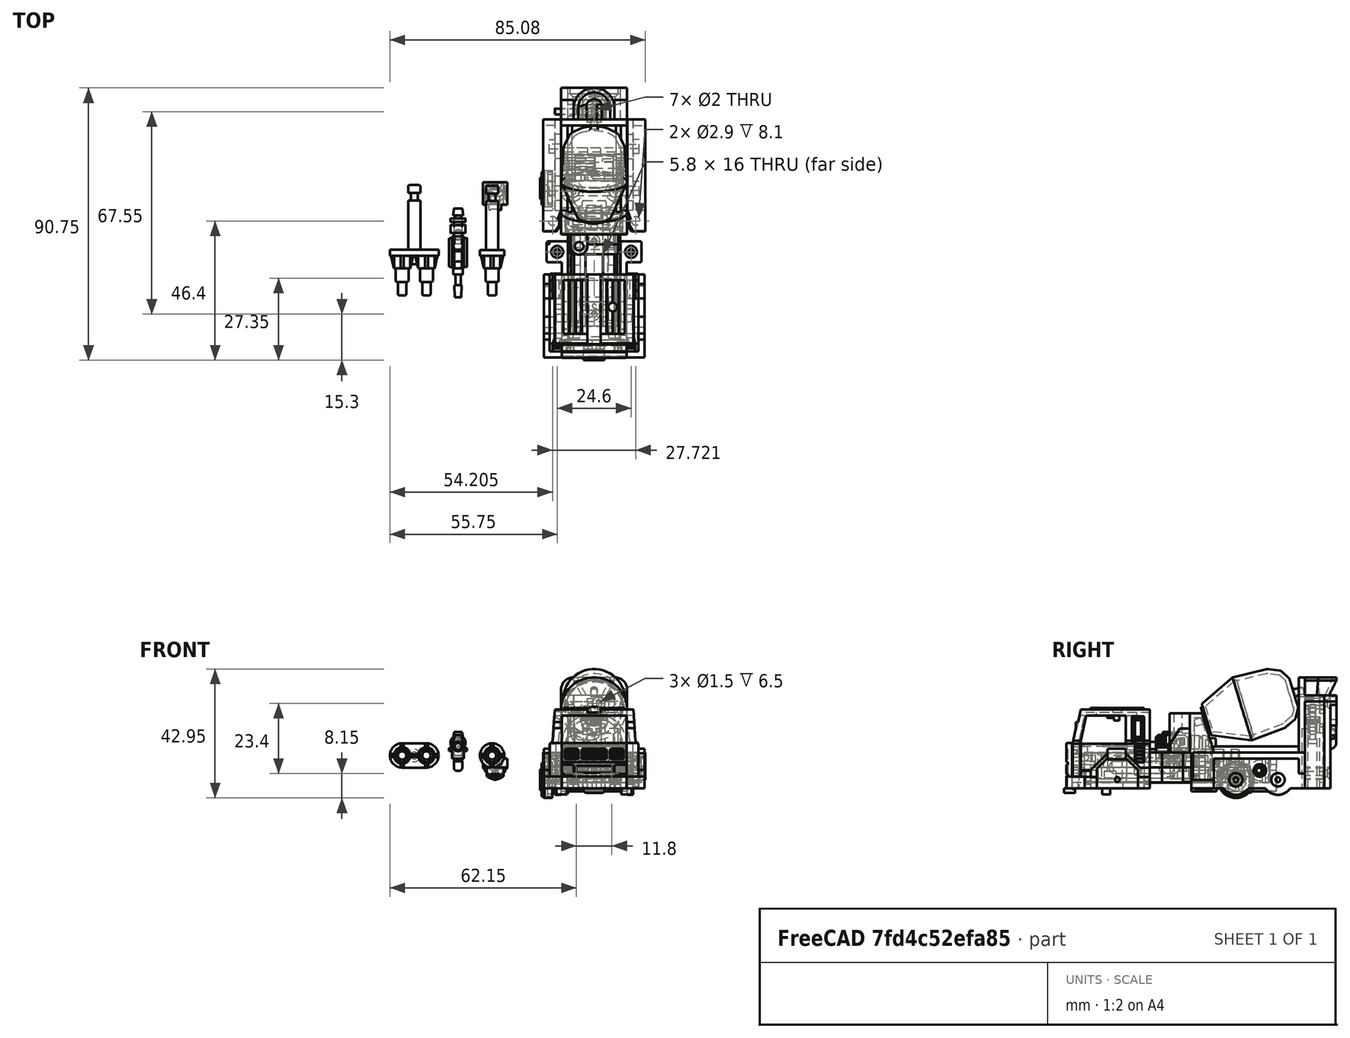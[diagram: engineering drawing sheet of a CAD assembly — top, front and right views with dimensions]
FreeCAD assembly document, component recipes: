
FREECAD ASSEMBLY — COMPONENT RECIPES ("MixMaster")

This assembly document has 25 components, labeled P0..P24 below (a component is one placed body or linked part). 24 of them carry a construction recipe — the FreeCAD feature program that regenerates the part from scratch, quoted from this document or its linked companion documents; the rest are supplied as boundary geometry only. No exploded tour is included for this assembly.
NOTE — document 2 of 4 of this assembly tour. The two overview renders and the header above are repeated from document 1; the component sections below continue where the previous document stopped.
COMPONENT P6 — recipe-attached ("top", modeled in this document).
Construction recipe (the document's own serialized feature program — sketch geometry with constraints, then the solid features built on it; lengths are millimeters unless a unit is written):

FEATURE [PartDesign::SubShapeBinder] Binder007
  BindCopyOnChange = 0
  BindMode = 2
  ClaimChildren = false
  Fuse = false
  MakeFace = true
  OffsetFill = false
  OffsetIntersection = false
  OffsetJoinType = 0
  OffsetOpenResult = false
  PartialLoad = false
  Refine = true
  Relative = true
  _Version = 2
FEATURE [Sketcher::SketchObject] Sketch141
  ArcFitTolerance = 1e-06
  AttachmentSupport = -> [Binder007]
  ExternalGeometry = -> [Binder007]
  FullyConstrained = true
  MakeInternals = false
  MapMode = 5
  Placement = pos=(5.89e-14,23,-1.557e-13) rot=(0,0.707107,0.707107;3.14159rad)
  sketch-geometry (8):
    g0: LineSegment StartX=-19.8 StartY=-11 StartZ=0 EndX=-19.8 EndY=18 EndZ=0
    g1: LineSegment StartX=-19.8 StartY=18 StartZ=0 EndX=-22 EndY=18 EndZ=0
    g2: LineSegment StartX=-19.8 StartY=-11 StartZ=0 EndX=-2.2 EndY=-11 EndZ=0
    g3: LineSegment StartX=-2.2 StartY=-11 StartZ=0 EndX=-2.2 EndY=18 EndZ=0
    g4: LineSegment StartX=-2.2 StartY=18 StartZ=0 EndX=0 EndY=18 EndZ=0
    g5: LineSegment StartX=0 StartY=18 StartZ=0 EndX=0 EndY=20 EndZ=0
    g6: LineSegment StartX=0 StartY=20 StartZ=0 EndX=-22 EndY=20 EndZ=0
    g7: LineSegment StartX=-22 StartY=20 StartZ=0 EndX=-22 EndY=18 EndZ=0
  constraints (21):
    c: Coincident(g0,g-3)
    c: Coincident(g0,g-3)
    c: Coincident(g1,g0)
    c: Horizontal(g1)
    c: DistanceX(g1,g1) = 2.2
    c: Coincident(g2,g0)
    c: Horizontal(g2)
    c: DistanceX(g2,g2) = 17.6
    c: Coincident(g3,g2)
    c: Vertical(g3)
    c: DistanceY(g3,g3) = 29
    c: Coincident(g4,g3)
    c: Horizontal(g4)
    c: DistanceX(g4,g4) = 2.2
    c: Coincident(g5,g4)
    c: Vertical(g5)
    c: DistanceY(g5,g5) = 2
    c: Coincident(g6,g5)
    c: Coincident(g6,g-4)
    c: Coincident(g7,g6)
    c: Coincident(g7,g1)
FEATURE [PartDesign::Pad] Pad114
  Direction = (2.6e-15,1,-6.7e-15)
  Length = 2
  Length2 = 10
  Profile = -> Sketch141
  ReferenceAxis = -> Sketch141 [N_Axis]
  Refine = true
  Suppressed = false
  Type = 0
FEATURE [Sketcher::SketchObject] Sketch142
  ArcFitTolerance = 1e-06
  AttachmentSupport = -> [Pad114]
  ExternalGeometry = -> [Pad114]
  FullyConstrained = true
  MakeInternals = false
  MapMode = 5
  Placement = pos=(5.82e-14,23,-1.559e-13) rot=(1,0,0;1.5708rad)
  sketch-geometry (8):
    g0: LineSegment StartX=14.75 StartY=-11 StartZ=0 EndX=14.75 EndY=10.5 EndZ=0
    g1: LineSegment StartX=14.75 StartY=10.5 StartZ=0 EndX=13.25 EndY=10.5 EndZ=0
    g2: LineSegment StartX=13.25 StartY=10.5 StartZ=0 EndX=13.25 EndY=-11 EndZ=0
    g3: LineSegment StartX=13.25 StartY=-11 StartZ=0 EndX=14.75 EndY=-11 EndZ=0
    g4: LineSegment StartX=8.75 StartY=-11 StartZ=0 EndX=8.75 EndY=10.5 EndZ=0
    g5: LineSegment StartX=8.75 StartY=10.5 StartZ=0 EndX=7.25 EndY=10.5 EndZ=0
    g6: LineSegment StartX=7.25 StartY=10.5 StartZ=0 EndX=7.25 EndY=-11 EndZ=0
    g7: LineSegment StartX=7.25 StartY=-11 StartZ=0 EndX=8.75 EndY=-11 EndZ=0
  constraints (24):
    c: PointOnObject(g0,g-3)
    c: Vertical(g0)
    c: Coincident(g1,g0)
    c: Horizontal(g1)
    c: Coincident(g2,g1)
    c: PointOnObject(g2,g-3)
    c: Vertical(g2)
    c: Coincident(g3,g2)
    c: Coincident(g3,g0)
    c: DistanceX(g0,g-3) = 5.05
    c: DistanceX(g2,g0) = 1.5
    c: DistanceY(g2,g2) = 21.5
    c: Coincident(g4,g5)
    c: Coincident(g5,g6)
    c: Coincident(g6,g7)
    c: Coincident(g7,g4)
    c: Vertical(g4)
    c: Vertical(g6)
    c: Horizontal(g5)
    c: Horizontal(g7)
    c: PointOnObject(g4,g-3)
    c: DistanceX(g7,g7) = 1.5
    c: DistanceX(g4,g2) = 4.5
    c: DistanceY(g6,g6) = 21.5
FEATURE [PartDesign::Pad] Pad115
  BaseFeature = -> Pad114
  Direction = (-2.5e-15,-1,6.7e-15)
  Length = 1.5
  Length2 = 10
  Profile = -> Sketch142
  ReferenceAxis = -> Sketch142 [N_Axis]
  Refine = true
  Suppressed = false
  Type = 0
FEATURE [Sketcher::SketchObject] Sketch143
  ArcFitTolerance = 1e-06
  AttachmentSupport = -> [Pad115]
  ExternalGeometry = -> [Pad115]
  FullyConstrained = true
  MakeInternals = false
  MapMode = 5
  Placement = pos=(5.82e-14,23,-1.559e-13) rot=(1,0,0;1.5708rad)
  sketch-geometry (8):
    g0: LineSegment StartX=11.75 StartY=-11 StartZ=0 EndX=10.25 EndY=-11 EndZ=0
    g1: LineSegment StartX=10.25 StartY=-11 StartZ=0 EndX=10.25 EndY=9 EndZ=0
    g2: LineSegment StartX=10.25 StartY=9 StartZ=0 EndX=8.75 EndY=9 EndZ=0
    g3: LineSegment StartX=8.75 StartY=9 StartZ=0 EndX=8.75 EndY=10.5 EndZ=0
    g4: LineSegment StartX=8.75 StartY=10.5 StartZ=0 EndX=13.25 EndY=10.5 EndZ=0
    g5: LineSegment StartX=13.25 StartY=10.5 StartZ=0 EndX=13.25 EndY=9 EndZ=0
    g6: LineSegment StartX=13.25 StartY=9 StartZ=0 EndX=11.75 EndY=9 EndZ=0
    g7: LineSegment StartX=11.75 StartY=9 StartZ=0 EndX=11.75 EndY=-11 EndZ=0
  constraints (22):
    c: PointOnObject(g0,g-3)
    c: PointOnObject(g0,g-3)
    c: Coincident(g1,g0)
    c: Vertical(g1)
    c: Coincident(g2,g1)
    c: PointOnObject(g2,g-4)
    c: Horizontal(g2)
    c: Coincident(g3,g2)
    c: Coincident(g3,g-4)
    c: Coincident(g4,g3)
    c: Coincident(g4,g-5)
    c: Coincident(g5,g4)
    c: PointOnObject(g5,g-5)
    c: Coincident(g6,g5)
    c: Horizontal(g6)
    c: Coincident(g7,g6)
    c: Coincident(g7,g0)
    c: Vertical(g7)
    c: DistanceX(g0,g0) = 1.5
    c: DistanceX(g-4,g0) = 1.5
    c: DistanceY(g3,g3) = 1.5
    c: DistanceY(g5,g5) = 1.5
FEATURE [PartDesign::Pad] Pad116
  BaseFeature = -> Pad115
  Direction = (-2.5e-15,-1,6.7e-15)
  Length = 0.5
  Length2 = 10
  Profile = -> Sketch143
  ReferenceAxis = -> Sketch143 [N_Axis]
  Refine = true
  Suppressed = false
  Type = 0
FEATURE [Sketcher::SketchObject] Sketch144
  ArcFitTolerance = 1e-06
  AttachmentSupport = -> [Pad116]
  ExternalGeometry = -> [Pad116]
  FullyConstrained = true
  MakeInternals = false
  MapMode = 5
  Placement = pos=(5.82e-14,23,-1.559e-13) rot=(1,0,0;1.5708rad)
  sketch-geometry (12):
    g0: LineSegment StartX=5.7 StartY=-11 StartZ=0 EndX=5.7 EndY=-9 EndZ=0
    g1: LineSegment StartX=5.7 StartY=-9 StartZ=0 EndX=4.2 EndY=-9 EndZ=0
    g2: LineSegment StartX=4.2 StartY=-9 StartZ=0 EndX=4.2 EndY=-11 EndZ=0
    g3: LineSegment StartX=4.2 StartY=-11 StartZ=0 EndX=5.7 EndY=-11 EndZ=0
    g4: LineSegment StartX=17.8 StartY=-11 StartZ=0 EndX=17.8 EndY=-9 EndZ=0
    g5: LineSegment StartX=17.8 StartY=-9 StartZ=0 EndX=16.3 EndY=-9 EndZ=0
    g6: LineSegment StartX=16.3 StartY=-9 StartZ=0 EndX=16.3 EndY=-11 EndZ=0
    g7: LineSegment StartX=16.3 StartY=-11 StartZ=0 EndX=17.8 EndY=-11 EndZ=0
    g8: LineSegment StartX=2.2 StartY=16.9 StartZ=0 EndX=2.2 EndY=9.5 EndZ=0
    g9: LineSegment StartX=2.2 StartY=9.5 StartZ=0 EndX=4.2 EndY=9.5 EndZ=0
    g10: LineSegment StartX=4.2 StartY=9.5 StartZ=0 EndX=4.2 EndY=16.9 EndZ=0
    g11: LineSegment StartX=4.2 StartY=16.9 StartZ=0 EndX=2.2 EndY=16.9 EndZ=0
  constraints (36):
    c: Coincident(g0,g1)
    c: Coincident(g1,g2)
    c: Coincident(g2,g3)
    c: Coincident(g3,g0)
    c: Vertical(g0)
    c: Vertical(g2)
    c: Horizontal(g1)
    c: Horizontal(g3)
    c: PointOnObject(g0,g-3)
    c: Coincident(g4,g5)
    c: Coincident(g5,g6)
    c: Coincident(g6,g7)
    c: Coincident(g7,g4)
    c: Vertical(g4)
    c: Vertical(g6)
    c: Horizontal(g5)
    c: Horizontal(g7)
    c: Coincident(g8,g9)
    c: Coincident(g9,g10)
    c: Coincident(g10,g11)
    c: Coincident(g11,g8)
    c: Vertical(g8)
    c: Vertical(g10)
    c: Horizontal(g9)
    c: Horizontal(g11)
    c: PointOnObject(g8,g-5)
    c: DistanceY(g8,g-5) = 1.1
    c: DistanceY(g8,g8) = 7.4
    c: DistanceX(g11,g11) = 2
    c: DistanceX(g3,g3) = 1.5
    c: DistanceY(g0,g0) = 2
    c: DistanceY(g6,g6) = 2
    c: DistanceX(g7,g7) = 1.5
    c: PointOnObject(g4,g-4)
    c: DistanceX(g-5,g2) = 2
    c: DistanceX(g4,g-4) = 2
FEATURE [PartDesign::Pad] Pad117
  BaseFeature = -> Pad116
  Direction = (-2.5e-15,-1,6.7e-15)
  Length = 1.5
  Length2 = 10
  Profile = -> Sketch144
  ReferenceAxis = -> Sketch144 [N_Axis]
  Refine = true
  Suppressed = false
  Type = 0
FEATURE [Sketcher::SketchObject] Sketch145
  ArcFitTolerance = 1e-06
  AttachmentSupport = -> [Pad117]
  ExternalGeometry = -> [Pad117]
  FullyConstrained = true
  MakeInternals = false
  MapMode = 5
  Placement = pos=(5.82e-14,23,-1.559e-13) rot=(1,0,0;1.5708rad)
  sketch-geometry (12):
    g0: LineSegment StartX=4.2 StartY=20 StartZ=0 EndX=4.2 EndY=18 EndZ=0
    g1: LineSegment StartX=4.2 StartY=18 StartZ=0 EndX=8.7 EndY=18 EndZ=0
    g2: LineSegment StartX=8.7 StartY=18 StartZ=0 EndX=8.7 EndY=19 EndZ=0
    g3: LineSegment StartX=8.7 StartY=19 StartZ=0 EndX=10.95 EndY=19 EndZ=0
    g4: LineSegment StartX=11.95 StartY=20 StartZ=0 EndX=4.2 EndY=20 EndZ=0
    g5: ArcOfCircle CenterX=10.95 CenterY=20 CenterZ=0 NormalX=0 NormalY=0 NormalZ=1 AngleXU=0 Radius=1 StartAngle=4.71239 EndAngle=6.28319
    g6: GeomPoint [constr] X=10.95 Y=19 Z=0
    g7: LineSegment StartX=17.8 StartY=20 StartZ=0 EndX=13.55 EndY=20 EndZ=0
    g8: LineSegment StartX=15.55 StartY=18 StartZ=0 EndX=17.8 EndY=18 EndZ=0
    g9: LineSegment StartX=17.8 StartY=18 StartZ=0 EndX=17.8 EndY=20 EndZ=0
    g10: ArcOfCircle CenterX=15.55 CenterY=20 CenterZ=0 NormalX=0 NormalY=0 NormalZ=1 AngleXU=0 Radius=2 StartAngle=3.14159 EndAngle=4.71239
    g11: GeomPoint [constr] X=15.55 Y=18 Z=0
  constraints (32):
    c: PointOnObject(g0,g-3)
    c: Vertical(g0)
    c: Coincident(g1,g0)
    c: Horizontal(g1)
    c: Coincident(g2,g1)
    c: Coincident(g3,g2)
    c: Horizontal(g3)
    c: Coincident(g4,g0)
    c: Horizontal(g4)
    c: Tangent(g3,g5) = -1.5708
    c: Coincident(g8,g9)
    c: Coincident(g9,g7)
    c: Horizontal(g7)
    c: Horizontal(g8)
    c: Vertical(g9)
    c: PointOnObject(g7,g-3)
    c: Tangent(g8,g10) = -1.5708
    c: DistanceY(g9,g9) = 2
    c: DistanceY(g0,g0) = 2
    c: Vertical(g2)
    c: DistanceX(g-3,g0) = 4.2
    c: DistanceX(g7,g-3) = 4.2
    c: Coincident(g10,g7)
    c: PointOnObject(g10,g7)
    c: DistanceX(g7,g7) = 4.25
    c: PointOnObject(g5,g4)
    c: DistanceX(g1,g1) = 4.5
    c: DistanceY(g2,g0) = 1
    c: DistanceX(g4,g4) = 7.75
    c: Coincident(g5,g4)
    c: Coincident(g6,g3)
    c: Coincident(g11,g8)
FEATURE [PartDesign::Pad] Pad118
  BaseFeature = -> Pad117
  Direction = (-2.5e-15,-1,6.7e-15)
  Length = 6.5
  Length2 = 10
  Profile = -> Sketch145
  ReferenceAxis = -> Sketch145 [N_Axis]
  Refine = true
  Suppressed = false
  Type = 0
FEATURE [Sketcher::SketchObject] Sketch146
  ArcFitTolerance = 1e-06
  AttachmentSupport = -> [Pad118]
  ExternalGeometry = -> [Pad118]
  FullyConstrained = true
  MakeInternals = false
  MapMode = 5
  Placement = pos=(5.82e-14,23,-1.559e-13) rot=(1,0,0;1.5708rad)
  sketch-geometry (9):
    g0: ArcOfCircle CenterX=12.5 CenterY=17.4 CenterZ=0 NormalX=0 NormalY=0 NormalZ=1 AngleXU=0 Radius=3.5 StartAngle=4.71239 EndAngle=6.28319
    g1: LineSegment StartX=8.7 StartY=19 StartZ=0 EndX=8.7 EndY=13.9 EndZ=0
    g2: LineSegment StartX=12.5 StartY=13.9 StartZ=0 EndX=8.7 EndY=13.9 EndZ=0
    g3: LineSegment StartX=8.7 StartY=19 StartZ=0 EndX=10.95 EndY=19 EndZ=0
    g4: ArcOfCircle CenterX=10.95 CenterY=20 CenterZ=0 NormalX=0 NormalY=0 NormalZ=1 AngleXU=0 Radius=1 StartAngle=4.71239 EndAngle=6.28319
    g5: LineSegment StartX=11.95 StartY=20 StartZ=0 EndX=13.55 EndY=20 EndZ=0
    g6: LineSegment StartX=16 StartY=17.4 StartZ=0 EndX=16 EndY=18 EndZ=0
    g7: LineSegment StartX=16 StartY=18 StartZ=0 EndX=15.55 EndY=18 EndZ=0
    g8: ArcOfCircle CenterX=15.55 CenterY=20 CenterZ=0 NormalX=0 NormalY=0 NormalZ=1 AngleXU=0 Radius=2 StartAngle=3.14159 EndAngle=4.71239
  constraints (25):
    c: Coincident(g1,g2)
    c: Coincident(g2,g0)
    c: Coincident(g0,g6)
    c: Coincident(g6,g7)
    c: Coincident(g7,g8)
    c: Coincident(g5,g8)
    c: Coincident(g4,g5)
    c: Coincident(g4,g3)
    c: Coincident(g3,g1)
    c: Coincident(g7,g-7)
    c: Coincident(g3,g-5)
    c: Coincident(g1,g-6)
    c: Vertical(g1)
    c: Horizontal(g7)
    c: Vertical(g6)
    c: Horizontal(g2)
    c: Radius(g0) = 3.5
    c: DistanceX(g0,g0) = 0
    c: DistanceY(g0,g0) = 0
    c: Coincident(g5,g-3)
    c: Coincident(g4,g-3)
    c: DistanceX(g7,g8) = 0
    c: DistanceX(g4,g3) = 0
    c: DistanceY(g0,g4) = 2.6
    c: DistanceX(g-6,g0) = 3.8
FEATURE [PartDesign::Pad] Pad119
  BaseFeature = -> Pad118
  Direction = (-2.5e-15,-1,6.7e-15)
  Length = 1.5
  Length2 = 10
  Profile = -> Sketch146
  ReferenceAxis = -> Sketch146 [N_Axis]
  Refine = true
  Suppressed = false
  Type = 0
FEATURE [Sketcher::SketchObject] Sketch147
  ArcFitTolerance = 1e-06
  AttachmentSupport = -> [Pad119]
  ExternalGeometry = -> [Pad119]
  FullyConstrained = true
  MakeInternals = false
  MapMode = 5
  Placement = pos=(5.25e-14,21.5,-1.441e-13) rot=(1,0,0;1.5708rad)
  sketch-geometry (1):
    g0: Circle CenterX=12.5 CenterY=17.4 CenterZ=0 NormalX=0 NormalY=0 NormalZ=1 AngleXU=0 Radius=2
  constraints (2):
    c: Coincident(g0,g-3)
    c: Radius(g0) = 2
FEATURE [PartDesign::Pocket] Pocket174
  BaseFeature = -> Pad119
  Direction = (2.4e-15,1,-6.7e-15)
  Length = 1.5
  Length2 = 5
  Profile = -> Sketch147
  ReferenceAxis = -> Sketch147 [N_Axis]
  Refine = true
  Suppressed = false
  Type = 0
FEATURE [Sketcher::SketchObject] Sketch148
  ArcFitTolerance = 1e-06
  AttachmentSupport = -> [Pocket174]
  ExternalGeometry = -> [Pocket174]
  FullyConstrained = true
  MakeInternals = false
  MapMode = 5
  Placement = pos=(5.82e-14,23,-1.559e-13) rot=(1,0,0;1.5708rad)
  sketch-geometry (3):
    g0: Circle CenterX=12.5 CenterY=17.4 CenterZ=0 NormalX=0 NormalY=0 NormalZ=1 AngleXU=0 Radius=1.15
    g1: Circle CenterX=5.1 CenterY=-6 CenterZ=0 NormalX=0 NormalY=0 NormalZ=1 AngleXU=0 Radius=1.15
    g2: Circle CenterX=16.9 CenterY=-6 CenterZ=0 NormalX=0 NormalY=0 NormalZ=1 AngleXU=0 Radius=1.15
  constraints (8):
    c: Coincident(g0,g-3)
    c: Diameter(g0) = 2.3
    c: DistanceX(g-6,g1) = 0.9
    c: DistanceX(g2,g-5) = 0.9
    c: DistanceY(g-5,g2) = 5
    c: DistanceY(g-6,g1) = 5
    c: Diameter(g1) = 2.3
    c: Diameter(g2) = 2.3
FEATURE [PartDesign::Pocket] Pocket175
  BaseFeature = -> Pocket174
  Direction = (2.5e-15,1,-6.7e-15)
  Length = 5
  Length2 = 5
  Profile = -> Sketch148
  ReferenceAxis = -> Sketch148 [N_Axis]
  Refine = true
  Suppressed = false
  Type = 0
FEATURE [Sketcher::SketchObject] Sketch149
  ArcFitTolerance = 1e-06
  AttachmentSupport = -> [Pocket175]
  ExternalGeometry = -> [Pocket175]
  FullyConstrained = true
  MakeInternals = false
  MapMode = 5
  Placement = pos=(6.33e-14,25,-1.695e-13) rot=(0,0.707107,0.707107;3.14159rad)
  sketch-geometry (6):
    g0: LineSegment StartX=-22 StartY=20 StartZ=0 EndX=-22 EndY=18 EndZ=0
    g1: LineSegment StartX=-22 StartY=18 StartZ=0 EndX=-13.4811 EndY=18 EndZ=0
    g2: LineSegment StartX=-22 StartY=20 StartZ=0 EndX=0 EndY=20 EndZ=0
    g3: LineSegment StartX=0 StartY=20 StartZ=0 EndX=-9e-16 EndY=18 EndZ=0
    g4: LineSegment StartX=-9e-16 StartY=18 StartZ=0 EndX=-11.5189 EndY=18 EndZ=0
    g5: ArcOfCircle CenterX=-12.5 CenterY=17.4 CenterZ=0 NormalX=0 NormalY=0 NormalZ=1 AngleXU=0 Radius=1.15 StartAngle=0.548888 EndAngle=2.5927
  constraints (14):
    c: Coincident(g0,g-7)
    c: Coincident(g0,g-7)
    c: Coincident(g1,g0)
    c: PointOnObject(g1,g-8)
    c: Horizontal(g1)
    c: Coincident(g2,g0)
    c: Coincident(g2,g-4)
    c: Coincident(g3,g2)
    c: Coincident(g3,g-5)
    c: PointOnObject(g4,g-8)
    c: Coincident(g4,g3)
    c: Coincident(g5,g1)
    c: Coincident(g5,g4)
    c: Coincident(g5,g-8)
FEATURE [PartDesign::Pad] Pad120
  BaseFeature = -> Pocket175
  Direction = (2.5e-15,1,-6.7e-15)
  Length = 2
  Length2 = 10
  Profile = -> Sketch149
  ReferenceAxis = -> Sketch149 [N_Axis]
  Refine = true
  Suppressed = false
  Type = 0
FEATURE [Sketcher::SketchObject] Sketch150
  ArcFitTolerance = 1e-06
  AttachmentSupport = -> [Pad120]
  ExternalGeometry = -> [Pad120]
  FullyConstrained = true
  MakeInternals = false
  MapMode = 5
  Placement = pos=(6.83e-14,27,-1.677e-13) rot=(0,0.707107,0.707107;3.14159rad)
  sketch-geometry (4):
    g0: ArcOfCircle CenterX=-12.5 CenterY=17.4 CenterZ=0 NormalX=0 NormalY=0 NormalZ=1 AngleXU=0 Radius=2.2 StartAngle=0.276227 EndAngle=2.86537
    g1: LineSegment StartX=-14.6166 StartY=18 StartZ=0 EndX=-13.4811 EndY=18 EndZ=0
    g2: LineSegment StartX=-10.3834 StartY=18 StartZ=0 EndX=-11.5189 EndY=18 EndZ=0
    g3: ArcOfCircle CenterX=-12.5 CenterY=17.4 CenterZ=0 NormalX=0 NormalY=0 NormalZ=1 AngleXU=0 Radius=1.15 StartAngle=0.548888 EndAngle=2.5927
  constraints (11):
    c: PointOnObject(g0,g-5)
    c: PointOnObject(g0,g-4)
    c: Radius(g0) = 2.2
    c: Coincident(g0,g-3)
    c: Coincident(g1,g0)
    c: Coincident(g1,g-5)
    c: Coincident(g2,g0)
    c: Coincident(g2,g-4)
    c: Coincident(g3,g1)
    c: Coincident(g3,g2)
    c: Tangent(g3,g-3)
FEATURE [PartDesign::Pocket] Pocket176
  BaseFeature = -> Pad120
  Direction = (-2.5e-15,-1,6.1e-15)
  Length = 2
  Length2 = 5
  Profile = -> Sketch150
  ReferenceAxis = -> Sketch150 [N_Axis]
  Refine = true
  Suppressed = false
  Type = 0
FEATURE [PartDesign::Hole] Hole
  BaseFeature = -> Pocket176
  CustomThreadClearance = 0
  Depth = 25
  DepthType = 0
  Diameter = 2.3
  DrillForDepth = false
  DrillPoint = 1
  DrillPointAngle = 118
  HoleCutCountersinkAngle = 90
  HoleCutCustomValues = false
  HoleCutDepth = 1.9
  HoleCutDiameter = 4.4
  HoleCutType = 2
  ModelThread = false
  Profile = -> Pocket176 [Edge166,Edge162,Edge163]
  Refine = true
  Suppressed = false
  Tapered = false
  TaperedAngle = 90
  ThreadClass = 0
  ThreadDepth = 25
  ThreadDepthType = 0
  ThreadDirection = 0
  ThreadFit = 0
  ThreadSize = 0
  ThreadType = 0
  Threaded = false
  UseCustomThreadClearance = false
FEATURE [PartDesign::Hole] Hole001
  BaseFeature = -> Hole
  CustomThreadClearance = 0
  Depth = 25
  DepthType = 0
  Diameter = 2.3
  DrillForDepth = false
  DrillPoint = 1
  DrillPointAngle = 118
  HoleCutCountersinkAngle = 90
  HoleCutCustomValues = false
  HoleCutDepth = 1.5
  HoleCutDiameter = 4.4
  HoleCutType = 2
  ModelThread = false
  Profile = -> Hole [Edge67,Edge66]
  Refine = true
  Suppressed = false
  Tapered = false
  TaperedAngle = 90
  ThreadClass = 0
  ThreadDepth = 25
  ThreadDepthType = 0
  ThreadDirection = 0
  ThreadFit = 0
  ThreadSize = 0
  ThreadType = 0
  Threaded = false
  UseCustomThreadClearance = false
FEATURE [Sketcher::SketchObject] Sketch151
  ArcFitTolerance = 1e-06
  AttachmentSupport = -> [Hole001]
  ExternalGeometry = -> [Hole001]
  FullyConstrained = true
  MakeInternals = false
  MapMode = 5
  Placement = pos=(6.28e-14,25,-1.715e-13) rot=(0,0.707107,0.707107;3.14159rad)
  sketch-geometry (4):
    g0: LineSegment StartX=-12.75 StartY=-4 StartZ=0 EndX=-12.75 EndY=-6 EndZ=0
    g1: LineSegment StartX=-12.75 StartY=-6 StartZ=0 EndX=-9.25 EndY=-6 EndZ=0
    g2: LineSegment StartX=-9.25 StartY=-6 StartZ=0 EndX=-9.25 EndY=-4 EndZ=0
    g3: LineSegment StartX=-9.25 StartY=-4 StartZ=0 EndX=-12.75 EndY=-4 EndZ=0
  constraints (13):
    c: Coincident(g0,g1)
    c: Coincident(g1,g2)
    c: Coincident(g2,g3)
    c: Coincident(g3,g0)
    c: Vertical(g0)
    c: Vertical(g2)
    c: Horizontal(g1)
    c: Horizontal(g3)
    c: DistanceX(g3,g3) = 3.5
    c: DistanceY(g0,g0) = 2
    c: DistanceY(g-3,g0) = 5
    c: DistanceX(g-3,g-3) = 17.6
    c: DistanceX(g-3,g0) = 7.05
FEATURE [PartDesign::Pocket] Pocket177
  BaseFeature = -> Hole001
  Direction = (-2.5e-15,-1,6.7e-15)
  Length = 1
  Length2 = 5
  Profile = -> Sketch151
  ReferenceAxis = -> Sketch151 [N_Axis]
  Refine = true
  Suppressed = false
  Type = 0
FEATURE [Sketcher::SketchObject] Sketch152
  ArcFitTolerance = 1e-06
  AttachmentSupport = -> [Pocket177]
  ExternalGeometry = -> [Pocket177]
  FullyConstrained = true
  MakeInternals = false
  MapMode = 5
  Placement = pos=(6.28e-14,25,-1.715e-13) rot=(0,0.707107,0.707107;3.14159rad)
  sketch-geometry (10):
    g0: LineSegment StartX=-19.8 StartY=16.9 StartZ=0 EndX=-12.9 EndY=10 EndZ=0
    g1: LineSegment StartX=-12.9 StartY=10 StartZ=0 EndX=-9.1 EndY=10 EndZ=0
    g2: LineSegment StartX=-9.1 StartY=10 StartZ=0 EndX=-2.2 EndY=16.9 EndZ=0
    g3: LineSegment StartX=-2.2 StartY=16.9 StartZ=0 EndX=-2.2 EndY=18 EndZ=0
    g4: LineSegment StartX=-2.2 StartY=18 StartZ=0 EndX=-3 EndY=18 EndZ=0
    g5: LineSegment StartX=-3 StartY=18 StartZ=0 EndX=-9 EndY=12 EndZ=0
    g6: LineSegment StartX=-9 StartY=12 StartZ=0 EndX=-13 EndY=12 EndZ=0
    g7: LineSegment StartX=-13 StartY=12 StartZ=0 EndX=-19 EndY=18 EndZ=0
    g8: LineSegment StartX=-19 StartY=18 StartZ=0 EndX=-19.8 EndY=18 EndZ=0
    g9: LineSegment StartX=-19.8 StartY=18 StartZ=0 EndX=-19.8 EndY=16.9 EndZ=0
  constraints (31):
    c: PointOnObject(g0,g-3)
    c: Coincident(g1,g0)
    c: Horizontal(g1)
    c: Coincident(g2,g1)
    c: PointOnObject(g2,g-4)
    c: Coincident(g3,g2)
    c: Coincident(g3,g-5)
    c: PointOnObject(g4,g3)
    c: PointOnObject(g4,g-5)
    c: Horizontal(g4)
    c: Coincident(g5,g4)
    c: Coincident(g6,g5)
    c: Coincident(g7,g6)
    c: PointOnObject(g7,g-6)
    c: PointOnObject(g8,g-3)
    c: Horizontal(g8)
    c: Parallel(g7,g0)
    c: Parallel(g5,g2)
    c: Parallel(g6,g1)
    c: Coincident(g8,g7)
    c: Coincident(g8,g9)
    c: Coincident(g0,g9)
    c: DistanceY(g0,g6) = 2
    c: DistanceX(g1,g1) = 3.8
    c: DistanceX(g6,g6) = 4
    c: Angle(g-5,g5) = 0.785398
    c: Angle(g7,g-6) = 0.785398
    c: DistanceX(g-7,g-7) = 17.6
    c: DistanceX(g-7,g0) = 6.9
    c: DistanceX(g8,g8) = 0.8
    c: DistanceX(g4,g4) = 0.8
FEATURE [PartDesign::Pad] Pad121
  BaseFeature = -> Pocket177
  Direction = (2.5e-15,1,-6.7e-15)
  Length = 2
  Length2 = 10
  Profile = -> Sketch152
  ReferenceAxis = -> Sketch152 [N_Axis]
  Refine = true
  Suppressed = false
  Type = 0
FEATURE [Sketcher::SketchObject] Sketch153
  ArcFitTolerance = 1e-06
  AttachmentSupport = -> [Pad121]
  ExternalGeometry = -> [Pad121]
  FullyConstrained = true
  MakeInternals = false
  MapMode = 5
  Placement = pos=(6.28e-14,25,-1.715e-13) rot=(0,0.707107,0.707107;3.14159rad)
  sketch-geometry (2):
    g0: LineSegment StartX=-11 StartY=10.8029 StartZ=0 EndX=-11 EndY=7.30294 EndZ=0
    g1: LineSegment StartX=-11 StartY=7.30294 StartZ=0 EndX=-2.2 EndY=4.1 EndZ=0
  constraints (8):
    c: Vertical(g0)
    c: Coincident(g1,g0)
    c: PointOnObject(g1,g-3)
    c: DistanceY(g1,g-3) = 12.8
    c: DistanceX(g-4,g-4) = 3.8
    c: DistanceX(g-4,g0) = 1.9
    c: Angle(g1,g-3) = 1.91986
    c: DistanceY(g0,g0) = 3.5
FEATURE [Sketcher::SketchObject] Sketch154
  ArcFitTolerance = 1e-06
  AttachmentSupport = -> [Pad121]
  ExternalGeometry = -> [Sketch153,Pad121]
  FullyConstrained = true
  MakeInternals = false
  MapMode = 5
  Placement = pos=(2.2,-5.4e-15,0) rot=(-0.57735,0.57735,0.57735;4.18879rad)
  sketch-geometry (2):
    g0: ArcOfCircle CenterX=-25 CenterY=4.1 CenterZ=0 NormalX=0 NormalY=0 NormalZ=1 AngleXU=0 Radius=1.9 StartAngle=1.5708 EndAngle=4.71239
    g1: LineSegment StartX=-25 StartY=6 StartZ=0 EndX=-25 EndY=2.2 EndZ=0
  constraints (6):
    c: PointOnObject(g0,g-4)
    c: Diameter(g0) = 3.8
    c: Coincident(g0,g-3)
    c: PointOnObject(g0,g-4)
    c: Coincident(g1,g0)
    c: Coincident(g1,g0)
FEATURE [PartDesign::AdditivePipe] AdditivePipe
  AuxilleryCurvelinear = true
  AuxillerySpineTangent = false
  BaseFeature = -> Pad121
  Binormal = (0,0,0)
  Mode = 0
  Profile = -> Sketch154
  Refine = true
  Spine = -> Sketch153 [Edge2,Edge1]
  SpineTangent = false
  Suppressed = false
  Transformation = 0
  Transition = 2
FEATURE [Sketcher::SketchObject] Sketch155
  ArcFitTolerance = 1e-06
  AttachmentSupport = -> [AdditivePipe]
  ExternalGeometry = -> [AdditivePipe]
  FullyConstrained = true
  MakeInternals = false
  MapMode = 5
  Placement = pos=(0,1.226e-13,20) rot=(0,0,1;0rad)
  sketch-geometry (8):
    g0: LineSegment StartX=13.55 StartY=21.5 StartZ=0 EndX=13.55 EndY=16.5 EndZ=0
    g1: LineSegment StartX=13.55 StartY=16.5 StartZ=0 EndX=15.05 EndY=16.5 EndZ=0
    g2: LineSegment StartX=15.05 StartY=16.5 StartZ=0 EndX=15.05 EndY=20.4704 EndZ=0
    g3: LineSegment StartX=6.95 StartY=20.4704 StartZ=0 EndX=6.95 EndY=16.5 EndZ=0
    g4: LineSegment StartX=6.95 StartY=16.5 StartZ=0 EndX=8.45 EndY=16.5 EndZ=0
    g5: LineSegment StartX=8.45 StartY=16.5 StartZ=0 EndX=8.45 EndY=21.5 EndZ=0
    g6: ArcOfCircle CenterX=11 CenterY=20.4704 CenterZ=0 NormalX=0 NormalY=0 NormalZ=1 AngleXU=0 Radius=2.75 StartAngle=0.383735 EndAngle=2.75786
    g7: ArcOfCircle CenterX=11 CenterY=20.4704 CenterZ=0 NormalX=0 NormalY=0 NormalZ=1 AngleXU=0 Radius=4.05 StartAngle=6.49071e-08 EndAngle=3.14159
  constraints (24):
    c: Coincident(g0,g-3)
    c: Coincident(g0,g-4)
    c: Coincident(g1,g0)
    c: PointOnObject(g1,g-4)
    c: Coincident(g2,g1)
    c: Vertical(g2)
    c: DistanceX(g1,g1) = 1.5
    c: PointOnObject(g3,g-5)
    c: Vertical(g3)
    c: Coincident(g4,g3)
    c: Vertical(g5)
    c: DistanceX(g-5,g3) = 2.75
    c: DistanceX(g4,g4) = 1.5
    c: Coincident(g5,g4)
    c: DistanceY(g-6,g-6) = 5
    c: Coincident(g6,g0)
    c: Coincident(g6,g5)
    c: Coincident(g7,g3)
    c: Coincident(g7,g2)
    c: Coincident(g7,g6)
    c: DistanceY(g5,g5) = 5
    c: PointOnObject(g4,g-5)
    c: DistanceY(g6,g3) = 0
    c: Radius(g6) = 2.75
FEATURE [Sketcher::SketchObject] Sketch156
  ArcFitTolerance = 1e-06
  AttachmentOffset = pos=(0,0,5) rot=(0,0,1;0rad)
  AttachmentSupport = -> [AdditivePipe]
  ExternalGeometry = -> [AdditivePipe]
  FullyConstrained = true
  MakeInternals = false
  MapMode = 5
  Placement = pos=(0,1.532e-13,25) rot=(0,0,1;0rad)
  sketch-geometry (8):
    g0: LineSegment StartX=17.8 StartY=16.5 StartZ=0 EndX=16.3 EndY=16.5 EndZ=0
    g1: LineSegment StartX=16.3 StartY=16.5 StartZ=0 EndX=16.3 EndY=20.7 EndZ=0
    g2: LineSegment StartX=4.2 StartY=16.5 StartZ=0 EndX=5.7 EndY=16.5 EndZ=0
    g3: LineSegment StartX=5.7 StartY=16.5 StartZ=0 EndX=5.7 EndY=20.7 EndZ=0
    g4: ArcOfCircle CenterX=11 CenterY=20.1598 CenterZ=0 NormalX=0 NormalY=0 NormalZ=1 AngleXU=0 Radius=5.32746 StartAngle=0.101567 EndAngle=3.04003
    g5: ArcOfCircle CenterX=11 CenterY=20.1598 CenterZ=0 NormalX=0 NormalY=0 NormalZ=1 AngleXU=0 Radius=6.84016 StartAngle=0.108421 EndAngle=3.03317
    g6: LineSegment StartX=17.8 StartY=20.9 StartZ=0 EndX=17.8 EndY=16.5 EndZ=0
    g7: LineSegment StartX=4.2 StartY=16.5 StartZ=0 EndX=4.2 EndY=20.9 EndZ=0
  constraints (24):
    c: PointOnObject(g0,g-6)
    c: Coincident(g1,g0)
    c: Vertical(g1)
    c: PointOnObject(g2,g-5)
    c: Coincident(g3,g2)
    c: Vertical(g3)
    c: Coincident(g4,g3)
    c: Coincident(g4,g1)
    c: PointOnObject(g5,g-4)
    c: PointOnObject(g5,g-3)
    c: Coincident(g4,g5)
    c: DistanceX(g-4,g-3) = 13.6
    c: DistanceX(g2,g4) = 6.8
    c: Tangent(g-7,g5)
    c: DistanceY(g3,g1) = 0
    c: DistanceX(g2,g2) = 1.5
    c: DistanceY(g3,g3) = 4.2
    c: DistanceY(g0,g5) = 4.4
    c: Coincident(g0,g-6)
    c: Coincident(g2,g-5)
    c: Coincident(g6,g0)
    c: Coincident(g6,g5)
    c: Coincident(g7,g2)
    c: Coincident(g7,g5)
FEATURE [PartDesign::AdditiveLoft] AdditiveLoft
  BaseFeature = -> AdditivePipe
  Closed = false
  Profile = -> Sketch155
  Refine = true
  Ruled = false
  Sections = -> [Sketch156]
  Suppressed = false
FEATURE [PartDesign::Pad] Pad122
  BaseFeature = -> AdditiveLoft
  Direction = (0,6.1e-15,1)
  Length = 1
  Length2 = 10
  Profile = -> Sketch156
  ReferenceAxis = -> Sketch156 [N_Axis]
  Refine = true
  Suppressed = false
  Type = 0
FEATURE [Sketcher::SketchObject] Sketch160
  ArcFitTolerance = 1e-06
  AttachmentSupport = -> [Pad122]
  ExternalGeometry = -> [Pad122]
  FullyConstrained = true
  MakeInternals = false
  MapMode = 5
  Placement = pos=(5.74e-14,21.5,-1.453e-13) rot=(1,0,0;1.5708rad)
  sketch-geometry (3):
    g0: LineSegment StartX=2.2 StartY=9.5 StartZ=0 EndX=4.2 EndY=9.5 EndZ=0
    g1: LineSegment StartX=4.2 StartY=9.5 StartZ=0 EndX=4.2 EndY=7.5 EndZ=0
    g2: LineSegment StartX=4.2 StartY=7.5 StartZ=0 EndX=2.2 EndY=9.5 EndZ=0
  constraints (7):
    c: Coincident(g0,g-3)
    c: Coincident(g0,g-3)
    c: Coincident(g1,g0)
    c: Vertical(g1)
    c: Coincident(g2,g1)
    c: Coincident(g2,g0)
    c: Angle(g2,g0) = 0.785398
FEATURE [PartDesign::Pad] Pad124
  BaseFeature = -> Pad122
  Direction = (-2.7e-15,-1,6.7e-15)
  Length = 1.5
  Length2 = 10
  Profile = -> Sketch160
  ReferenceAxis = -> Sketch160 [N_Axis]
  Refine = true
  Reversed = true
  Suppressed = false
  Type = 0
FEATURE [Sketcher::SketchObject] Sketch303
  ArcFitTolerance = 1e-06
  AttachmentSupport = -> [Pad124]
  ExternalGeometry = -> [Pad124]
  FullyConstrained = true
  MakeInternals = false
  MapMode = 5
  Placement = pos=(5.25e-14,21.5,-1.441e-13) rot=(1,0,0;1.5708rad)
  sketch-geometry (1):
    g0: Circle CenterX=12.5 CenterY=17.4 CenterZ=0 NormalX=0 NormalY=0 NormalZ=1 AngleXU=0 Radius=2.025
  constraints (2):
    c: Coincident(g0,g-3)
    c: Diameter(g0) = 4.05
FEATURE [PartDesign::Pocket] Pocket211
  BaseFeature = -> Pad124
  Direction = (2.4e-15,1,-6.7e-15)
  Length = 1.5
  Length2 = 5
  Profile = -> Sketch303
  ReferenceAxis = -> Sketch303 [N_Axis]
  Refine = true
  Suppressed = false
  Type = 0
FEATURE [PartDesign::Pocket] Pocket212
  BaseFeature = -> Pocket211
  Direction = (2.4e-15,1,-6.7e-15)
  Length = 5
  Length2 = 5
  Profile = -> Sketch303
  ReferenceAxis = -> Sketch303 [N_Axis]
  Refine = true
  Reversed = true
  Suppressed = false
  Type = 0
FEATURE [Sketcher::SketchObject] Sketch304
  ArcFitTolerance = 1e-06
  AttachmentSupport = -> [Pocket212]
  ExternalGeometry = -> [Pocket212]
  FullyConstrained = true
  MakeInternals = false
  MapMode = 5
  Placement = pos=(5.25e-14,21.5,-1.441e-13) rot=(1,0,0;1.5708rad)
  sketch-geometry (1):
    g0: Circle CenterX=12.5 CenterY=17.4 CenterZ=0 NormalX=0 NormalY=0 NormalZ=1 AngleXU=0 Radius=2.05
  constraints (3):
    c: Radius(g-3) = 2.025
    c: Coincident(g0,g-3)
    c: Radius(g0) = 2.05
FEATURE [PartDesign::Pocket] Pocket213
  BaseFeature = -> Pocket212
  Direction = (2.4e-15,1,-6.7e-15)
  Length = 1.55
  Length2 = 5
  Profile = -> Sketch304
  ReferenceAxis = -> Sketch304 [N_Axis]
  Refine = true
  Suppressed = false
  Type = 0
FEATURE [PartDesign::Pocket] Pocket214
  BaseFeature = -> Pocket213
  Direction = (2.4e-15,1,-6.7e-15)
  Length = 5
  Length2 = 5
  Profile = -> Sketch304
  ReferenceAxis = -> Sketch304 [N_Axis]
  Refine = true
  Reversed = true
  Suppressed = false
  Type = 0
FEATURE [Sketcher::SketchObject] Sketch305
  ArcFitTolerance = 1e-06
  AttachmentSupport = -> [Pocket214]
  ExternalGeometry = -> [Pocket214]
  FullyConstrained = true
  MakeInternals = false
  MapMode = 5
  Placement = pos=(6.84e-14,21.5,-1.419e-13) rot=(1,0,0;1.5708rad)
  sketch-geometry (4):
    g0: LineSegment StartX=2.2 StartY=9.5 StartZ=0 EndX=4.2 EndY=7.5 EndZ=0
    g1: LineSegment StartX=4.2 StartY=7.5 StartZ=0 EndX=4.2 EndY=7.6 EndZ=0
    g2: LineSegment StartX=4.2 StartY=7.6 StartZ=0 EndX=2.2 EndY=9.6 EndZ=0
    g3: LineSegment StartX=2.2 StartY=9.6 StartZ=0 EndX=2.2 EndY=9.5 EndZ=0
  constraints (10):
    c: Coincident(g0,g-4)
    c: Coincident(g0,g-5)
    c: Coincident(g1,g0)
    c: PointOnObject(g1,g-5)
    c: Coincident(g2,g1)
    c: PointOnObject(g2,g-4)
    c: Coincident(g3,g2)
    c: Coincident(g3,g0)
    c: Parallel(g2,g0)
    c: DistanceY(g1,g1) = 0.1
FEATURE [PartDesign::Body] Body015  label="top"
  AllowCompound = false
  Group = -> [Binder007,Sketch141,Pad114,Sketch142,Pad115,Sketch143,Pad116,Sketch144,Pad117,Sketch145,Pad118,Sketch146,Pad119,Sketch147,Pocket174,Sketch148,Pocket175,Sketch149,Pad120,Sketch150,Pocket176,Hole,Hole001,Sketch151,Pocket177,Sketch152,Pad121,Sketch153,Sketch154,AdditivePipe,Sketch155,Sketch156,AdditiveLoft,Pad122,Sketch160,Pad124,Sketch303,Pocket211,Pocket212,Sketch304,Pocket213,Pocket214,Sketch305,+1 more]
  Origin = -> Origin017
  Placement = pos=(33,19,9e-16) rot=(0,0,1;0rad)
  Tip = -> Pocket215
COMPONENT P7 — recipe-attached ("Trigger", modeled in this document).
Construction recipe (the document's own serialized feature program — sketch geometry with constraints, then the solid features built on it; lengths are millimeters unless a unit is written):

FEATURE [PartDesign::SubShapeBinder] Binder020
  BindCopyOnChange = 0
  BindMode = 2
  ClaimChildren = false
  Context = -> Body016 [Binder020.]
  Fuse = false
  MakeFace = true
  OffsetFill = false
  OffsetIntersection = false
  OffsetJoinType = 0
  OffsetOpenResult = false
  PartialLoad = false
  Refine = true
  Relative = true
  _Version = 2
FEATURE [Sketcher::SketchObject] Sketch157
  ArcFitTolerance = 1e-06
  AttachmentSupport = -> [Binder020]
  ExternalGeometry = -> [Binder020]
  FullyConstrained = true
  MakeInternals = false
  MapMode = 5
  Placement = pos=(2.47e-14,18,-1.562e-13) rot=(0,0.707107,0.707107;3.14159rad)
  sketch-geometry (2):
    g0: Circle CenterX=-8 CenterY=15 CenterZ=0 NormalX=0 NormalY=0 NormalZ=1 AngleXU=0 Radius=1
    g1: Circle CenterX=-8 CenterY=15 CenterZ=0 NormalX=0 NormalY=0 NormalZ=1 AngleXU=0 Radius=2
  constraints (4):
    c: Coincident(g0,g-3)
    c: Radius(g0) = 1
    c: Coincident(g1,g0)
    c: Radius(g1) = 2
FEATURE [PartDesign::Pad] Pad123
  Direction = (1.4e-15,1,-8.7e-15)
  Length = 2
  Length2 = 10
  Profile = -> Sketch157
  ReferenceAxis = -> Sketch157 [N_Axis]
  Refine = true
  Suppressed = false
  Type = 0
FEATURE [Sketcher::SketchObject] Sketch158
  ArcFitTolerance = 1e-06
  AttachmentSupport = -> [Pad123]
  ExternalGeometry = -> [Pad123]
  FullyConstrained = true
  MakeInternals = false
  MapMode = 5
  Placement = pos=(2.64e-14,20,-1.64e-13) rot=(0,0.707107,0.707107;3.14159rad)
  sketch-geometry (22):
    g0: LineSegment StartX=-6.05 StartY=14.5556 StartZ=0 EndX=1.85 EndY=14.5556 EndZ=0
    g1: LineSegment StartX=2.05 StartY=14.3556 StartZ=0 EndX=2.05 EndY=13.2626 EndZ=0
    g2: LineSegment StartX=1.88095 StartY=12.936 StartZ=0 EndX=-4.95 EndY=8.10559 EndZ=0
    g3: LineSegment StartX=-4.95 StartY=8.10559 StartZ=0 EndX=-4.95 EndY=6.35559 EndZ=0
    g4: LineSegment StartX=-5.95 StartY=5.35559 StartZ=0 EndX=-7.95 EndY=5.35559 EndZ=0
    g5: LineSegment StartX=-8.17361 StartY=5.49379 StartZ=0 EndX=-8.72361 EndY=6.59379 EndZ=0
    g6: LineSegment StartX=-8.5 StartY=6.95559 StartZ=0 EndX=-7.25 EndY=6.95559 EndZ=0
    g7: LineSegment StartX=-7.25 StartY=6.95559 StartZ=0 EndX=-7.25 EndY=12.9556 EndZ=0
    g8: LineSegment StartX=-7.25 StartY=12.9556 StartZ=0 EndX=-14.95 EndY=12.9556 EndZ=0
    g9: LineSegment StartX=-14.95 StartY=12.9556 StartZ=0 EndX=-14.95 EndY=14.5556 EndZ=0
    g10: LineSegment StartX=-14.95 StartY=14.5556 StartZ=0 EndX=-9.95 EndY=14.5556 EndZ=0
    g11: ArcOfCircle CenterX=-8.5 CenterY=6.70559 CenterZ=0 NormalX=0 NormalY=0 NormalZ=1 AngleXU=0 Radius=0.25 StartAngle=1.5708 EndAngle=3.60524
    g12: GeomPoint [constr] X=-8.90451 Y=6.95559 Z=0
    g13: ArcOfCircle CenterX=-7.95 CenterY=5.60559 CenterZ=0 NormalX=0 NormalY=0 NormalZ=1 AngleXU=0 Radius=0.25 StartAngle=3.60524 EndAngle=4.71239
    g14: GeomPoint [constr] X=-8.10451 Y=5.35559 Z=0
    g15: ArcOfCircle CenterX=-5.95 CenterY=6.35559 CenterZ=0 NormalX=0 NormalY=0 NormalZ=1 AngleXU=0 Radius=1 StartAngle=4.71239 EndAngle=6.28319
    g16: GeomPoint [constr] X=-4.95 Y=5.35559 Z=0
    g17: ArcOfCircle CenterX=-8 CenterY=15 CenterZ=0 NormalX=0 NormalY=0 NormalZ=1 AngleXU=0 Radius=2 StartAngle=3.36567 EndAngle=6.05911
    g18: ArcOfCircle CenterX=1.85 CenterY=14.3556 CenterZ=0 NormalX=0 NormalY=0 NormalZ=1 AngleXU=0 Radius=0.2 StartAngle=2.9e-15 EndAngle=1.5708
    g19: GeomPoint [constr] X=2.05 Y=14.5556 Z=0
    g20: ArcOfCircle CenterX=1.65 CenterY=13.2626 CenterZ=0 NormalX=0 NormalY=0 NormalZ=1 AngleXU=0 Radius=0.4 StartAngle=5.32789 EndAngle=6.28319
    g21: GeomPoint [constr] X=2.05 Y=13.0556 Z=0
  constraints (56):
    c: PointOnObject(g0,g-4)
    c: Horizontal(g0)
    c: Vertical(g1)
    c: Coincident(g3,g2)
    c: Vertical(g3)
    c: Coincident(g7,g6)
    c: Vertical(g7)
    c: Coincident(g8,g7)
    c: Horizontal(g8)
    c: Coincident(g9,g8)
    c: Vertical(g9)
    c: Coincident(g10,g9)
    c: Horizontal(g10)
    c: DistanceX(g9,g19) = 17
    c: DistanceY(g21,g19) = 1.5
    c: Horizontal(g4)
    c: DistanceX(g8,g8) = 7.7
    c: PointOnObject(g12,g5)
    c: PointOnObject(g12,g6)
    c: Tangent(g5,g11) = 1.5708
    c: Tangent(g6,g11) = 1.5708
    c: PointOnObject(g14,g4)
    c: PointOnObject(g14,g5)
    c: Tangent(g4,g13) = 1.5708
    c: Tangent(g5,g13) = 1.5708
    c: Horizontal(g6)
    c: DistanceX(g6,g2) = 2.3
    c: DistanceY(g4,g6) = 1.6
    c: PointOnObject(g16,g3)
    c: PointOnObject(g16,g4)
    c: Tangent(g3,g15) = 1.5708
    c: Tangent(g4,g15) = 1.5708
    c: DistanceY(g4,g2) = 2.75
    c: DistanceY(g7,g7) = 6
    c: DistanceX(g10,g10) = 5
    c: DistanceX(g-4,g7) = 0.75
    c: Coincident(g17,g10)
    c: Coincident(g17,g0)
    c: Coincident(g17,g-4)
    c: DistanceY(g10,g0) = 0
    c: DistanceY(g9,g9) = 1.6
    c: PointOnObject(g19,g0)
    c: PointOnObject(g19,g1)
    c: Tangent(g0,g18) = 1.5708
    c: Tangent(g1,g18) = 1.5708
    c: PointOnObject(g21,g1)
    c: PointOnObject(g21,g2)
    c: Tangent(g1,g20) = 1.5708
    c: Tangent(g2,g20) = 1.5708
    c: Radius(g18) = 0.2
    c: Radius(g20) = 0.4
    c: Radius(g15) = 1
    c: Radius(g11) = 0.25
    c: Radius(g13) = 0.25
    c: DistanceX(g6,g6) = 1.25
    c: DistanceX(g4,g4) = 2
FEATURE [PartDesign::Pad] Pad125
  BaseFeature = -> Pad123
  Direction = (1.3e-15,1,-8.3e-15)
  Length = 2
  Length2 = 10
  Profile = -> Sketch158
  ReferenceAxis = -> Sketch158 [N_Axis]
  Refine = true
  Reversed = true
  Suppressed = false
  Type = 0
FEATURE [Sketcher::SketchObject] Sketch161
  ArcFitTolerance = 1e-06
  AttachmentSupport = -> [Pad125]
  ExternalGeometry = -> [Pad125]
  FullyConstrained = true
  MakeInternals = false
  MapMode = 5
  Placement = pos=(0,1.071e-13,12.9556) rot=(1,0,0;3.14159rad)
  sketch-geometry (1):
    g0: Circle CenterX=11 CenterY=-19 CenterZ=0 NormalX=0 NormalY=0 NormalZ=1 AngleXU=0 Radius=0.75
  constraints (4):
    c: Diameter(g0) = 1.5
    c: DistanceY(g-3,g-3) = 2
    c: DistanceY(g-3,g0) = 1
    c: DistanceX(g0,g-3) = 3.95
FEATURE [PartDesign::Pad] Pad126
  BaseFeature = -> Pad125
  Direction = (0,-8.3e-15,-1)
  Length = 1.5
  Length2 = 10
  Profile = -> Sketch161
  ReferenceAxis = -> Sketch161 [N_Axis]
  Refine = true
  Suppressed = false
  Type = 0
FEATURE [PartDesign::Fillet] Fillet
  Base = -> Pad126 [Edge59]
  BaseFeature = -> Pad126
  Radius = 0.5
  Refine = true
  SupportTransform = false
  Suppressed = false
  UseAllEdges = false
FEATURE [PartDesign::Fillet] Fillet001
  Base = -> Fillet [Edge44,Edge15]
  BaseFeature = -> Fillet
  Radius = 0.7
  Refine = true
  SupportTransform = false
  Suppressed = false
  UseAllEdges = false
FEATURE [PartDesign::Body] Body016  label="Trigger"
  AllowCompound = false
  Group = -> [Binder020,Sketch157,Pad123,Sketch158,Pad125,Sketch161,Pad126,Fillet,Fillet001]
  Origin = -> Origin018
  Placement = pos=(33,19.1,7.1e-15) rot=(0,0,1;0rad)
  Tip = -> Fillet001
COMPONENT P8 — recipe-attached ("Rear Legs", modeled in this document).
Construction recipe (the document's own serialized feature program — sketch geometry with constraints, then the solid features built on it; lengths are millimeters unless a unit is written):

FEATURE [PartDesign::SubShapeBinder] Binder019
  BindCopyOnChange = 0
  BindMode = 2
  ClaimChildren = false
  Context = -> Body018 [Binder019.]
  Fuse = false
  MakeFace = true
  OffsetFill = false
  OffsetIntersection = false
  OffsetJoinType = 0
  OffsetOpenResult = false
  PartialLoad = false
  Refine = true
  Relative = true
  _Version = 2
FEATURE [Sketcher::SketchObject] Sketch171
  ArcFitTolerance = 1e-06
  AttachmentSupport = -> [Binder019]
  ExternalGeometry = -> [Binder019]
  FullyConstrained = true
  MakeInternals = false
  MapMode = 5
  Placement = pos=(3.78e-14,0,-4) rot=(0,0,1;0rad)
  sketch-geometry (24):
    g0: ArcOfCircle CenterX=7.5 CenterY=-13.05 CenterZ=0 NormalX=0 NormalY=0 NormalZ=1 AngleXU=0 Radius=0.5 StartAngle=1.5708 EndAngle=3.14159
    g1: LineSegment StartX=7.5 StartY=-12.55 StartZ=0 EndX=14.5 EndY=-12.55 EndZ=0
    g2: ArcOfCircle CenterX=14.5 CenterY=-13.05 CenterZ=0 NormalX=0 NormalY=0 NormalZ=1 AngleXU=0 Radius=0.499996 StartAngle=6.28318 EndAngle=7.85399
    g3: LineSegment StartX=15 StartY=-13.05 StartZ=0 EndX=15 EndY=-16.95 EndZ=0
    g4: LineSegment StartX=15 StartY=-16.95 StartZ=0 EndX=19.2 EndY=-16.95 EndZ=0
    g5: ArcOfCircle CenterX=19.2 CenterY=-17.45 CenterZ=0 NormalX=0 NormalY=0 NormalZ=1 AngleXU=0 Radius=0.500005 StartAngle=1.09474e-05 EndAngle=1.57079
    g6: LineSegment StartX=19.7 StartY=-17.45 StartZ=0 EndX=19.7 EndY=-22.95 EndZ=0
    g7: LineSegment StartX=19.7 StartY=-22.95 StartZ=0 EndX=19.8 EndY=-22.95 EndZ=0
    g8: LineSegment StartX=19.8 StartY=-22.95 StartZ=0 EndX=19.8 EndY=-54.45 EndZ=0
    g9: LineSegment StartX=7 StartY=-13.05 StartZ=0 EndX=7 EndY=-16.95 EndZ=0
    g10: LineSegment StartX=7 StartY=-16.95 StartZ=0 EndX=2.8 EndY=-16.95 EndZ=0
    g11: ArcOfCircle CenterX=2.80001 CenterY=-17.45 CenterZ=0 NormalX=0 NormalY=0 NormalZ=1 AngleXU=0 Radius=0.500006 StartAngle=1.57081 EndAngle=3.14158
    g12: LineSegment StartX=2.3 StartY=-17.45 StartZ=0 EndX=2.3 EndY=-22.95 EndZ=0
    g13: LineSegment StartX=2.3 StartY=-22.95 StartZ=0 EndX=2.2 EndY=-22.95 EndZ=0
    g14: LineSegment StartX=2.2 StartY=-22.95 StartZ=0 EndX=2.2 EndY=-54.45 EndZ=0
    g15: LineSegment StartX=19.8 StartY=-54.45 StartZ=0 EndX=17.55 EndY=-54.45 EndZ=0
    g16: LineSegment StartX=17.55 StartY=-54.45 StartZ=0 EndX=17.55 EndY=-55.575 EndZ=0
    g17: LineSegment StartX=15.8 StartY=-55.575 StartZ=0 EndX=15.8 EndY=-54.45 EndZ=0
    g18: LineSegment StartX=15.8 StartY=-54.45 StartZ=0 EndX=6.2 EndY=-54.45 EndZ=0
    g19: LineSegment StartX=6.2 StartY=-54.45 StartZ=0 EndX=6.2 EndY=-55.575 EndZ=0
    g20: LineSegment StartX=4.45 StartY=-55.575 StartZ=0 EndX=4.45 EndY=-54.45 EndZ=0
    g21: LineSegment StartX=4.45 StartY=-54.45 StartZ=0 EndX=2.2 EndY=-54.45 EndZ=0
    g22: ArcOfCircle CenterX=5.325 CenterY=-55.575 CenterZ=0 NormalX=0 NormalY=0 NormalZ=1 AngleXU=0 Radius=0.875 StartAngle=3.14159 EndAngle=6.28319
    g23: ArcOfCircle CenterX=16.675 CenterY=-55.575 CenterZ=0 NormalX=0 NormalY=0 NormalZ=1 AngleXU=0 Radius=0.875 StartAngle=3.14159 EndAngle=6.28319
  constraints (63):
    c: Coincident(g0,g-6)
    c: Tangent(g0,g-5) = -1.5708
    c: Coincident(g1,g0)
    c: Coincident(g1,g-7)
    c: Coincident(g2,g1)
    c: Coincident(g2,g-8)
    c: Coincident(g4,g3)
    c: Coincident(g4,g-10)
    c: Coincident(g5,g4)
    c: Coincident(g5,g-11)
    c: Coincident(g3,g-9)
    c: Coincident(g3,g2)
    c: Tangent(g2,g-7)
    c: Tangent(g5,g-10)
    c: Coincident(g7,g6)
    c: Coincident(g7,g-18)
    c: Coincident(g8,g7)
    c: Vertical(g8)
    c: Coincident(g6,g5)
    c: Coincident(g6,g-17)
    c: Coincident(g9,g0)
    c: Coincident(g9,g-12)
    c: Coincident(g10,g9)
    c: Coincident(g10,g-13)
    c: Coincident(g11,g10)
    c: Coincident(g11,g-14)
    c: Tangent(g11,g-13)
    c: Coincident(g13,g12)
    c: Coincident(g13,g-16)
    c: Coincident(g14,g13)
    c: Vertical(g14)
    c: Coincident(g15,g8)
    c: Horizontal(g15)
    c: Coincident(g16,g15)
    c: PointOnObject(g17,g-3)
    c: Coincident(g18,g17)
    c: PointOnObject(g18,g-3)
    c: Coincident(g19,g18)
    c: Vertical(g20)
    c: Coincident(g21,g20)
    c: Coincident(g21,g14)
    c: Horizontal(g21)
    c: DistanceX(g15,g15) = 2.25
    c: DistanceX(g21,g21) = 2.25
    c: DistanceX(g20,g18) = 1.75
    c: DistanceX(g17,g15) = 1.75
    c: DistanceY(g15,g-3) = 0
    c: DistanceY(g20,g-3) = 0
    c: Vertical(g19)
    c: Coincident(g22,g20)
    c: Coincident(g22,g19)
    c: DistanceY(g19,g22) = 0
    c: DistanceY(g20,g22) = 0
    c: DistanceY(g19,g18) = 1.125
    c: Coincident(g23,g17)
    c: Coincident(g23,g16)
    c: DistanceY(g23,g17) = 1.125
    c: DistanceY(g16,g23) = 0
    c: DistanceY(g17,g23) = 0
    c: Vertical(g16)
    c: Vertical(g17)
    c: Coincident(g12,g11)
    c: Coincident(g12,g-15)
FEATURE [PartDesign::Pad] Pad134
  Direction = (-9.5e-15,0,1)
  Length = 4.8
  Length2 = 10
  Profile = -> Sketch171
  ReferenceAxis = -> Sketch171 [N_Axis]
  Refine = true
  Suppressed = false
  Type = 0
FEATURE [Sketcher::SketchObject] Sketch172
  ArcFitTolerance = 1e-06
  AttachmentSupport = -> [Pad134]
  ExternalGeometry = -> [Binder019]
  FullyConstrained = true
  MakeInternals = false
  MapMode = 5
  Placement = pos=(3.78e-14,0,-4) rot=(1,0,0;3.14159rad)
  sketch-geometry (4):
    g0: LineSegment StartX=8.1 StartY=46.35 StartZ=0 EndX=8.1 EndY=30.35 EndZ=0
    g1: LineSegment StartX=8.1 StartY=30.35 StartZ=0 EndX=13.9 EndY=30.35 EndZ=0
    g2: LineSegment StartX=13.9 StartY=30.35 StartZ=0 EndX=13.9 EndY=46.35 EndZ=0
    g3: LineSegment StartX=13.9 StartY=46.35 StartZ=0 EndX=8.1 EndY=46.35 EndZ=0
  constraints (12):
    c: Coincident(g0,g1)
    c: Coincident(g1,g2)
    c: Coincident(g2,g3)
    c: Coincident(g3,g0)
    c: Vertical(g0)
    c: Vertical(g2)
    c: Horizontal(g1)
    c: Horizontal(g3)
    c: DistanceY(g0,g-3) = 8.1
    c: DistanceX(g-3,g0) = 3.4
    c: DistanceX(g3,g3) = 5.8
    c: DistanceY(g0,g0) = 16
FEATURE [PartDesign::Pocket] Pocket161
  BaseFeature = -> Pad134
  Direction = (-9.5e-15,0,1)
  Length = 5
  Length2 = 5
  Profile = -> Sketch172
  ReferenceAxis = -> Sketch172 [N_Axis]
  Refine = true
  Suppressed = false
  Type = 0
FEATURE [Sketcher::SketchObject] Sketch173
  ArcFitTolerance = 1e-06
  AttachmentSupport = -> [Pocket161]
  ExternalGeometry = -> [Pocket161]
  FullyConstrained = true
  MakeInternals = false
  MapMode = 5
  Placement = pos=(-7.6e-15,0,0.8) rot=(0,0,1;0rad)
  sketch-geometry (6):
    g0: LineSegment StartX=7 StartY=-16.95 StartZ=0 EndX=7 EndY=-13.05 EndZ=0
    g1: LineSegment StartX=15 StartY=-13.05 StartZ=0 EndX=15 EndY=-16.95 EndZ=0
    g2: LineSegment StartX=15 StartY=-16.95 StartZ=0 EndX=7 EndY=-16.95 EndZ=0
    g3: ArcOfCircle CenterX=7.5 CenterY=-13.05 CenterZ=0 NormalX=0 NormalY=0 NormalZ=1 AngleXU=0 Radius=0.5 StartAngle=1.5708 EndAngle=3.14159
    g4: ArcOfCircle CenterX=14.5 CenterY=-13.05 CenterZ=0 NormalX=0 NormalY=0 NormalZ=1 AngleXU=0 Radius=0.499996 StartAngle=6.28318 EndAngle=7.85399
    g5: LineSegment StartX=7.5 StartY=-12.55 StartZ=0 EndX=14.5 EndY=-12.55 EndZ=0
  constraints (12):
    c: Coincident(g0,g-5)
    c: Coincident(g0,g-5)
    c: Coincident(g1,g-7)
    c: Coincident(g1,g-7)
    c: Coincident(g2,g1)
    c: Coincident(g2,g0)
    c: Coincident(g3,g0)
    c: Tangent(g3,g-4) = -1.5708
    c: Coincident(g4,g1)
    c: Tangent(g4,g-6) = -1.5708
    c: Coincident(g5,g3)
    c: Coincident(g5,g4)
FEATURE [PartDesign::Pocket] Pocket162
  BaseFeature = -> Pocket161
  Direction = (9.5e-15,0,-1)
  Length = 1.8
  Length2 = 5
  Profile = -> Sketch173
  ReferenceAxis = -> Sketch173 [N_Axis]
  Refine = true
  Suppressed = false
  Type = 0
FEATURE [Sketcher::SketchObject] Sketch174
  ArcFitTolerance = 1e-06
  AttachmentSupport = -> [Pocket162]
  ExternalGeometry = -> [Pocket162]
  FullyConstrained = true
  MakeInternals = false
  MapMode = 5
  Placement = pos=(-7.6e-15,0,0.8) rot=(0,0,1;0rad)
  sketch-geometry (8):
    g0: LineSegment StartX=8.1 StartY=-30.35 StartZ=0 EndX=13.9 EndY=-30.35 EndZ=0
    g1: LineSegment StartX=13.9 StartY=-30.35 StartZ=0 EndX=13.9 EndY=-16.95 EndZ=0
    g2: LineSegment StartX=8.1 StartY=-30.35 StartZ=0 EndX=8.1 EndY=-16.95 EndZ=0
    g3: LineSegment StartX=13.9 StartY=-16.95 StartZ=0 EndX=8.1 EndY=-16.95 EndZ=0
    g4: LineSegment StartX=8.1 StartY=-46.35 StartZ=0 EndX=13.9 EndY=-46.35 EndZ=0
    g5: LineSegment StartX=8.1 StartY=-46.35 StartZ=0 EndX=8.1 EndY=-54.45 EndZ=0
    g6: LineSegment StartX=13.9 StartY=-46.35 StartZ=0 EndX=13.9 EndY=-54.45 EndZ=0
    g7: LineSegment StartX=13.9 StartY=-54.45 StartZ=0 EndX=8.1 EndY=-54.45 EndZ=0
  constraints (20):
    c: Coincident(g0,g-3)
    c: Coincident(g0,g-3)
    c: Coincident(g1,g0)
    c: PointOnObject(g1,g-4)
    c: Vertical(g1)
    c: Coincident(g2,g0)
    c: PointOnObject(g2,g-4)
    c: Vertical(g2)
    c: Coincident(g3,g1)
    c: Coincident(g3,g2)
    c: Coincident(g4,g-5)
    c: Coincident(g4,g-5)
    c: Coincident(g5,g4)
    c: PointOnObject(g5,g-6)
    c: Vertical(g5)
    c: Coincident(g6,g4)
    c: PointOnObject(g6,g-6)
    c: Vertical(g6)
    c: Coincident(g7,g6)
    c: Coincident(g7,g5)
FEATURE [PartDesign::Pocket] Pocket163
  BaseFeature = -> Pocket162
  Direction = (9.5e-15,0,-1)
  Length = 0.8
  Length2 = 5
  Profile = -> Sketch174
  ReferenceAxis = -> Sketch174 [N_Axis]
  Refine = true
  Suppressed = false
  Type = 0
FEATURE [Sketcher::SketchObject] Sketch175
  ArcFitTolerance = 1e-06
  AttachmentSupport = -> [Pocket163]
  ExternalGeometry = -> [Pocket163]
  FullyConstrained = true
  MakeInternals = false
  MapMode = 5
  Placement = pos=(0,0,3.98e-14) rot=(0,0,1;0rad)
  sketch-geometry (1):
    g0: Circle CenterX=11 CenterY=-47.6 CenterZ=0 NormalX=0 NormalY=0 NormalZ=1 AngleXU=0 Radius=0.625
  constraints (4):
    c: Diameter(g0) = 1.25
    c: DistanceX(g-3,g-3) = 5.8
    c: DistanceX(g-3,g0) = 2.9
    c: DistanceY(g0,g-3) = 1.25
FEATURE [PartDesign::Pocket] Pocket164
  BaseFeature = -> Pocket163
  Direction = (9.5e-15,0,-1)
  Length = 0.5
  Length2 = 5
  Profile = -> Sketch175
  ReferenceAxis = -> Sketch175 [N_Axis]
  Refine = true
  Suppressed = false
  Type = 0
FEATURE [Sketcher::SketchObject] Sketch176
  ArcFitTolerance = 1e-06
  AttachmentSupport = -> [Pocket164]
  ExternalGeometry = -> [Pocket164]
  FullyConstrained = true
  MakeInternals = false
  MapMode = 5
  Placement = pos=(-7.6e-15,0,0.8) rot=(0,0,1;0rad)
  sketch-geometry (8):
    g0: LineSegment StartX=3.3 StartY=-17.45 StartZ=0 EndX=3.3 EndY=-53.95 EndZ=0
    g1: LineSegment StartX=4.3 StartY=-53.95 StartZ=0 EndX=4.3 EndY=-17.45 EndZ=0
    g2: ArcOfCircle CenterX=3.8 CenterY=-17.45 CenterZ=0 NormalX=0 NormalY=0 NormalZ=1 AngleXU=0 Radius=0.5 StartAngle=9e-16 EndAngle=3.14159
    g3: ArcOfCircle CenterX=3.8 CenterY=-53.95 CenterZ=0 NormalX=0 NormalY=0 NormalZ=1 AngleXU=0 Radius=0.5 StartAngle=3.14159 EndAngle=6.28319
    g4: LineSegment StartX=17.7 StartY=-53.95 StartZ=0 EndX=17.7 EndY=-17.45 EndZ=0
    g5: LineSegment StartX=18.7 StartY=-17.45 StartZ=0 EndX=18.7 EndY=-53.95 EndZ=0
    g6: ArcOfCircle CenterX=18.2 CenterY=-53.95 CenterZ=0 NormalX=0 NormalY=0 NormalZ=1 AngleXU=0 Radius=0.5 StartAngle=3.14159 EndAngle=6.28319
    g7: ArcOfCircle CenterX=18.2 CenterY=-17.45 CenterZ=0 NormalX=0 NormalY=0 NormalZ=1 AngleXU=0 Radius=0.5 StartAngle=1.1e-15 EndAngle=3.14159
  constraints (28):
    c: Vertical(g0)
    c: Vertical(g1)
    c: Coincident(g2,g0)
    c: Coincident(g2,g1)
    c: Coincident(g3,g1)
    c: Coincident(g3,g0)
    c: Vertical(g4)
    c: Vertical(g5)
    c: Coincident(g6,g4)
    c: Coincident(g6,g5)
    c: Coincident(g7,g5)
    c: Coincident(g7,g4)
    c: Tangent(g7,g-4)
    c: Tangent(g6,g-5)
    c: Tangent(g3,g-6)
    c: Tangent(g2,g-3)
    c: Diameter(g2) = 1
    c: Diameter(g7) = 1
    c: DistanceY(g2,g1) = 0
    c: DistanceY(g2,g0) = 0
    c: DistanceY(g3,g1) = 0
    c: DistanceY(g3,g0) = 0
    c: DistanceY(g6,g4) = 0
    c: DistanceY(g6,g5) = 0
    c: DistanceY(g7,g4) = 0
    c: DistanceY(g7,g5) = 0
    c: DistanceX(g5,g-5) = 1.1
    c: DistanceX(g-6,g0) = 1.1
FEATURE [PartDesign::Pad] Pad135
  BaseFeature = -> Pocket164
  Direction = (-9.5e-15,0,1)
  Length = 0.2
  Length2 = 10
  Profile = -> Sketch176
  ReferenceAxis = -> Sketch176 [N_Axis]
  Refine = true
  Suppressed = false
  Type = 0
FEATURE [Sketcher::SketchObject] Sketch177
  ArcFitTolerance = 1e-06
  AttachmentSupport = -> [Pad135]
  ExternalGeometry = -> [Pad135]
  FullyConstrained = true
  MakeInternals = false
  MapMode = 5
  Placement = pos=(3.78e-14,0,-4) rot=(1,0,0;3.14159rad)
  sketch-geometry (44):
    g0: LineSegment StartX=18.2 StartY=18.45 StartZ=0 EndX=3.8 EndY=18.45 EndZ=0
    g1: LineSegment StartX=3.8 StartY=18.45 StartZ=0 EndX=3.8 EndY=26.95 EndZ=0
    g2: LineSegment StartX=3.8 StartY=26.95 StartZ=0 EndX=4 EndY=26.95 EndZ=0
    g3: LineSegment StartX=4.25 StartY=27.2 StartZ=0 EndX=4.25 EndY=31.1 EndZ=0
    g4: LineSegment StartX=4 StartY=31.35 StartZ=0 EndX=3.7 EndY=31.35 EndZ=0
    g5: LineSegment StartX=3.7 StartY=31.35 StartZ=0 EndX=3.7 EndY=45.35 EndZ=0
    g6: LineSegment StartX=3.7 StartY=45.35 StartZ=0 EndX=4 EndY=45.35 EndZ=0
    g7: LineSegment StartX=4.25 StartY=45.6 StartZ=0 EndX=4.25 EndY=49.5 EndZ=0
    g8: LineSegment StartX=4 StartY=49.75 StartZ=0 EndX=3.7 EndY=49.75 EndZ=0
    g9: LineSegment StartX=3.7 StartY=49.75 StartZ=0 EndX=3.7 EndY=52.45 EndZ=0
    g10: LineSegment StartX=3.7 StartY=52.45 StartZ=0 EndX=6.2 EndY=52.45 EndZ=0
    g11: LineSegment StartX=6.2 StartY=52.45 StartZ=0 EndX=6.2 EndY=22.65 EndZ=0
    g12: LineSegment StartX=7.4 StartY=21.45 StartZ=0 EndX=14.6 EndY=21.45 EndZ=0
    g13: LineSegment StartX=18.2 StartY=18.45 StartZ=0 EndX=18.2 EndY=26.95 EndZ=0
    g14: LineSegment StartX=18.2 StartY=26.95 StartZ=0 EndX=18 EndY=26.95 EndZ=0
    g15: LineSegment StartX=17.75 StartY=27.2 StartZ=0 EndX=17.75 EndY=31.1 EndZ=0
    g16: LineSegment StartX=18 StartY=31.35 StartZ=0 EndX=18.3 EndY=31.35 EndZ=0
    g17: LineSegment StartX=18.3 StartY=31.35 StartZ=0 EndX=18.3 EndY=45.35 EndZ=0
    g18: LineSegment StartX=18.3 StartY=45.35 StartZ=0 EndX=18 EndY=45.35 EndZ=0
    g19: LineSegment StartX=17.75 StartY=45.6 StartZ=0 EndX=17.75 EndY=49.5 EndZ=0
    g20: LineSegment StartX=18 StartY=49.75 StartZ=0 EndX=18.3 EndY=49.75 EndZ=0
    g21: LineSegment StartX=18.3 StartY=49.75 StartZ=0 EndX=18.3 EndY=52.45 EndZ=0
    g22: LineSegment StartX=18.3 StartY=52.45 StartZ=0 EndX=15.8 EndY=52.45 EndZ=0
    g23: LineSegment StartX=15.8 StartY=52.45 StartZ=0 EndX=15.8 EndY=22.65 EndZ=0
    g24: ArcOfCircle CenterX=14.6 CenterY=22.65 CenterZ=0 NormalX=0 NormalY=0 NormalZ=1 AngleXU=0 Radius=1.2 StartAngle=4.71239 EndAngle=6.28319
    g25: GeomPoint [constr] X=15.8 Y=21.45 Z=0
    g26: ArcOfCircle CenterX=7.4 CenterY=22.65 CenterZ=0 NormalX=0 NormalY=0 NormalZ=1 AngleXU=0 Radius=1.2 StartAngle=3.14159 EndAngle=4.71239
    g27: GeomPoint [constr] X=6.2 Y=21.45 Z=0
    g28: ArcOfCircle CenterX=4 CenterY=27.2 CenterZ=0 NormalX=0 NormalY=0 NormalZ=1 AngleXU=0 Radius=0.25 StartAngle=4.71239 EndAngle=6.28319
    g29: GeomPoint [constr] X=4.25 Y=26.95 Z=0
    g30: ArcOfCircle CenterX=4 CenterY=31.1 CenterZ=0 NormalX=0 NormalY=0 NormalZ=1 AngleXU=0 Radius=0.25 StartAngle=1.9e-15 EndAngle=1.5708
    g31: GeomPoint [constr] X=4.25 Y=31.35 Z=0
    g32: ArcOfCircle CenterX=18 CenterY=31.1 CenterZ=0 NormalX=0 NormalY=0 NormalZ=1 AngleXU=0 Radius=0.25 StartAngle=1.5708 EndAngle=3.14159
    g33: GeomPoint [constr] X=17.75 Y=31.35 Z=0
    g34: ArcOfCircle CenterX=18 CenterY=27.2 CenterZ=0 NormalX=0 NormalY=0 NormalZ=1 AngleXU=0 Radius=0.25 StartAngle=3.14159 EndAngle=4.71239
    g35: GeomPoint [constr] X=17.75 Y=26.95 Z=0
    g36: ArcOfCircle CenterX=18 CenterY=45.6 CenterZ=0 NormalX=0 NormalY=0 NormalZ=1 AngleXU=0 Radius=0.25 StartAngle=3.14159 EndAngle=4.71239
    g37: GeomPoint [constr] X=17.75 Y=45.35 Z=0
    g38: ArcOfCircle CenterX=18 CenterY=49.5 CenterZ=0 NormalX=0 NormalY=0 NormalZ=1 AngleXU=0 Radius=0.25 StartAngle=1.5708 EndAngle=3.14159
    g39: GeomPoint [constr] X=17.75 Y=49.75 Z=0
    g40: ArcOfCircle CenterX=4 CenterY=49.5 CenterZ=0 NormalX=0 NormalY=0 NormalZ=1 AngleXU=0 Radius=0.25 StartAngle=-9e-16 EndAngle=1.5708
    g41: GeomPoint [constr] X=4.25 Y=49.75 Z=0
    g42: ArcOfCircle CenterX=4 CenterY=45.6 CenterZ=0 NormalX=0 NormalY=0 NormalZ=1 AngleXU=0 Radius=0.25 StartAngle=4.71239 EndAngle=6.28319
    g43: GeomPoint [constr] X=4.25 Y=45.35 Z=0
  constraints (113):
    c: Horizontal(g0)
    c: Coincident(g1,g0)
    c: Vertical(g1)
    c: Coincident(g2,g1)
    c: Vertical(g3)
    c: Horizontal(g4)
    c: Coincident(g5,g4)
    c: Vertical(g5)
    c: Coincident(g6,g5)
    c: Horizontal(g6)
    c: Vertical(g7)
    c: Coincident(g9,g8)
    c: Vertical(g9)
    c: Coincident(g10,g9)
    c: Horizontal(g10)
    c: Coincident(g11,g10)
    c: Vertical(g11)
    c: Horizontal(g12)
    c: Coincident(g13,g0)
    c: Coincident(g14,g13)
    c: Horizontal(g14)
    c: Horizontal(g16)
    c: Coincident(g17,g16)
    c: Vertical(g17)
    c: Coincident(g18,g17)
    c: Vertical(g19)
    c: Coincident(g21,g20)
    c: Coincident(g22,g21)
    c: Horizontal(g22)
    c: Coincident(g23,g22)
    c: Vertical(g23)
    c: PointOnObject(g25,g12)
    c: PointOnObject(g25,g23)
    c: Tangent(g12,g24) = -1.5708
    c: Tangent(g23,g24) = 1.5708
    c: PointOnObject(g27,g11)
    c: PointOnObject(g27,g12)
    c: Tangent(g11,g26) = -1.5708
    c: Tangent(g12,g26) = -1.5708
    c: PointOnObject(g29,g2)
    c: PointOnObject(g29,g3)
    c: Tangent(g2,g28) = -1.5708
    c: Tangent(g3,g28) = -1.5708
    c: PointOnObject(g31,g3)
    c: PointOnObject(g31,g4)
    c: Tangent(g3,g30) = -1.5708
    c: Tangent(g4,g30) = -1.5708
    c: PointOnObject(g33,g15)
    c: PointOnObject(g33,g16)
    c: Tangent(g15,g32) = 1.5708
    c: Tangent(g16,g32) = 1.5708
    c: PointOnObject(g35,g14)
    c: PointOnObject(g35,g15)
    c: Tangent(g14,g34) = 1.5708
    c: Tangent(g15,g34) = 1.5708
    c: PointOnObject(g37,g18)
    c: PointOnObject(g37,g19)
    c: Tangent(g18,g36) = 1.5708
    c: Tangent(g19,g36) = 1.5708
    c: PointOnObject(g39,g19)
    c: PointOnObject(g39,g20)
    c: Tangent(g19,g38) = 1.5708
    c: Tangent(g20,g38) = 1.5708
    c: PointOnObject(g41,g7)
    c: PointOnObject(g41,g8)
    c: Tangent(g7,g40) = -1.5708
    c: Tangent(g8,g40) = -1.5708
    c: PointOnObject(g43,g6)
    c: PointOnObject(g43,g7)
    c: Tangent(g6,g42) = -1.5708
    c: Tangent(g7,g42) = -1.5708
    c: DistanceY(g-8,g0) = 1.5
    c: DistanceX(g0,g-7) = 1.5
    c: DistanceX(g-10,g0) = 1.5
    c: Vertical(g15)
    c: DistanceY(g9,g-3) = 2
    c: DistanceY(g21,g-5) = 2
    c: Vertical(g21)
    c: DistanceX(g19,g20) = 0.55
    c: Diameter(g38) = 0.5
    c: Diameter(g36) = 0.5
    c: Horizontal(g18)
    c: Horizontal(g8)
    c: Horizontal(g2)
    c: Vertical(g13)
    c: Diameter(g32) = 0.5
    c: Diameter(g34) = 0.5
    c: Diameter(g28) = 0.5
    c: Diameter(g30) = 0.5
    c: Diameter(g42) = 0.5
    c: Diameter(g40) = 0.5
    c: DistanceX(g8,g7) = 0.55
    c: DistanceX(g-4,g9) = 1.5
    c: DistanceX(g21,g-6) = 1.5
    c: DistanceX(g22,g22) = 2.5
    c: DistanceX(g10,g10) = 2.5
    c: DistanceY(g0,g12) = 3
    c: Radius(g24) = 1.2
    c: Radius(g26) = 1.2
    c: DistanceX(g-4,g4) = 1.5
    c: DistanceX(g16,g-6) = 1.5
    c: DistanceY(g17,g20) = 4.4
    c: DistanceY(g5,g8) = 4.4
    c: DistanceY(g1,g4) = 4.4
    c: DistanceY(g13,g16) = 4.4
    c: DistanceX(g15,g13) = 0.45
    c: DistanceX(g1,g3) = 0.45
    c: Horizontal(g20)
    c: DistanceY(g13,g13) = 8.5
    c: DistanceY(g1,g1) = 8.5
    c: DistanceY(g5,g5) = 14
    c: DistanceY(g17,g17) = 14
    c: DistanceX(g-4,g-10) = 0.1
FEATURE [PartDesign::Pocket] Pocket165
  BaseFeature = -> Pad135
  Direction = (-9.5e-15,0,1)
  Length = 3.2
  Length2 = 5
  Profile = -> Sketch177
  ReferenceAxis = -> Sketch177 [N_Axis]
  Refine = true
  Suppressed = false
  Type = 0
FEATURE [Sketcher::SketchObject] Sketch178
  ArcFitTolerance = 1e-06
  AttachmentSupport = -> [Pocket165]
  ExternalGeometry = -> [Pocket165]
  FullyConstrained = true
  MakeInternals = false
  MapMode = 5
  Placement = pos=(2.2,0,2.08e-14) rot=(0.57735,-0.57735,-0.57735;2.0944rad)
  sketch-geometry (4):
    g0: ArcOfCircle CenterX=29.35 CenterY=-4 CenterZ=0 NormalX=0 NormalY=0 NormalZ=1 AngleXU=0 Radius=2.2 StartAngle=1.5708 EndAngle=3.14159
    g1: ArcOfCircle CenterX=48.25 CenterY=-4 CenterZ=0 NormalX=0 NormalY=0 NormalZ=1 AngleXU=0 Radius=2.2 StartAngle=-9e-16 EndAngle=1.5708
    g2: LineSegment StartX=29.35 StartY=-1.8 StartZ=0 EndX=48.25 EndY=-1.8 EndZ=0
    g3: LineSegment StartX=50.45 StartY=-4 StartZ=0 EndX=27.15 EndY=-4 EndZ=0
  constraints (14):
    c: PointOnObject(g0,g-5)
    c: PointOnObject(g1,g-5)
    c: Coincident(g2,g0)
    c: Coincident(g2,g1)
    c: Horizontal(g2)
    c: Coincident(g3,g1)
    c: Coincident(g3,g0)
    c: Radius(g0) = 2.2
    c: Radius(g1) = 2.2
    c: DistanceX(g1,g1) = 0
    c: DistanceX(g0,g0) = 0
    c: DistanceX(g-5,g0) = 4.2
    c: PointOnObject(g0,g3)
    c: DistanceX(g1,g-5) = 4
FEATURE [PartDesign::Pocket] Pocket166
  BaseFeature = -> Pocket165
  Direction = (1,-1e-16,9.4e-15)
  Length = 3
  Length2 = 5
  Profile = -> Sketch178
  ReferenceAxis = -> Sketch178 [N_Axis]
  Refine = true
  Suppressed = false
  Type = 0
FEATURE [Sketcher::SketchObject] Sketch179
  ArcFitTolerance = 1e-06
  AttachmentSupport = -> [Pocket166]
  ExternalGeometry = -> [Pocket166]
  FullyConstrained = true
  MakeInternals = false
  MapMode = 5
  Placement = pos=(0,-52.45,0) rot=(0,0.707107,0.707107;3.14159rad)
  sketch-geometry (4):
    g0: LineSegment StartX=-4.7 StartY=-1.8 StartZ=0 EndX=-4.7 EndY=-4 EndZ=0
    g1: LineSegment StartX=-4.7 StartY=-4 StartZ=0 EndX=-3.7 EndY=-4 EndZ=0
    g2: LineSegment StartX=-4.7 StartY=-1.8 StartZ=0 EndX=-3.7 EndY=-1.8 EndZ=0
    g3: LineSegment StartX=-3.7 StartY=-1.8 StartZ=0 EndX=-3.7 EndY=-4 EndZ=0
  constraints (11):
    c: Coincident(g0,g1)
    c: Horizontal(g1)
    c: Vertical(g0)
    c: Coincident(g2,g0)
    c: PointOnObject(g2,g-3)
    c: Coincident(g3,g2)
    c: Coincident(g3,g1)
    c: Horizontal(g2)
    c: DistanceY(g2,g-4) = 1
    c: DistanceX(g2,g2) = 1
    c: Coincident(g1,g-3)
FEATURE [PartDesign::Pocket] Pocket167
  BaseFeature = -> Pocket166
  Direction = (0,-1,2e-16)
  Length = 16
  Length2 = 5
  Profile = -> Sketch179
  ReferenceAxis = -> Sketch179 [N_Axis]
  Refine = true
  Reversed = true
  Suppressed = false
  Type = 0
FEATURE [Sketcher::SketchObject] Sketch180
  ArcFitTolerance = 1e-06
  AttachmentSupport = -> [Pocket167]
  ExternalGeometry = -> [Pocket167]
  FullyConstrained = true
  MakeInternals = false
  MapMode = 5
  Placement = pos=(0,-18.45,0) rot=(1,0,0;1.5708rad)
  sketch-geometry (4):
    g0: LineSegment StartX=3.8 StartY=-4 StartZ=0 EndX=4.8 EndY=-4 EndZ=0
    g1: LineSegment StartX=4.8 StartY=-4 StartZ=0 EndX=4.8 EndY=-1.8 EndZ=0
    g2: LineSegment StartX=4.8 StartY=-1.8 StartZ=0 EndX=3.8 EndY=-1.8 EndZ=0
    g3: LineSegment StartX=3.8 StartY=-1.8 StartZ=0 EndX=3.8 EndY=-4 EndZ=0
  constraints (11):
    c: Coincident(g0,g1)
    c: Coincident(g1,g2)
    c: Coincident(g2,g3)
    c: Coincident(g3,g0)
    c: Horizontal(g0)
    c: Horizontal(g2)
    c: Vertical(g1)
    c: Vertical(g3)
    c: Coincident(g0,g-5)
    c: DistanceY(g2,g-4) = 1
    c: DistanceX(g2,g2) = 1
FEATURE [PartDesign::Pocket] Pocket168
  BaseFeature = -> Pocket167
  Direction = (0,1,-2e-16)
  Length = 13
  Length2 = 5
  Profile = -> Sketch180
  ReferenceAxis = -> Sketch180 [N_Axis]
  Refine = true
  Reversed = true
  Suppressed = false
  Type = 0
FEATURE [Sketcher::SketchObject] Sketch181
  ArcFitTolerance = 1e-06
  AttachmentSupport = -> [Pocket168]
  ExternalGeometry = -> [Pocket168]
  FullyConstrained = true
  MakeInternals = false
  MapMode = 5
  Placement = pos=(19.8,0,1.873e-13) rot=(0.57735,0.57735,0.57735;2.0944rad)
  sketch-geometry (4):
    g0: ArcOfCircle CenterX=-48.25 CenterY=-4 CenterZ=0 NormalX=0 NormalY=0 NormalZ=1 AngleXU=0 Radius=2.2 StartAngle=1.5708 EndAngle=3.14159
    g1: ArcOfCircle CenterX=-29.35 CenterY=-4 CenterZ=0 NormalX=0 NormalY=0 NormalZ=1 AngleXU=0 Radius=2.2 StartAngle=0 EndAngle=1.5708
    g2: LineSegment StartX=-48.25 StartY=-1.8 StartZ=0 EndX=-29.35 EndY=-1.8 EndZ=0
    g3: LineSegment StartX=-27.15 StartY=-4 StartZ=0 EndX=-50.45 EndY=-4 EndZ=0
  constraints (14):
    c: PointOnObject(g0,g-3)
    c: PointOnObject(g1,g-3)
    c: Coincident(g2,g0)
    c: Coincident(g2,g1)
    c: Horizontal(g2)
    c: Coincident(g3,g1)
    c: Coincident(g3,g0)
    c: Radius(g0) = 2.2
    c: Radius(g1) = 2.2
    c: DistanceX(g0,g0) = 0
    c: DistanceX(g1,g1) = 0
    c: PointOnObject(g1,g3)
    c: DistanceX(g-3,g0) = 4
    c: DistanceX(g1,g-3) = 4.2
FEATURE [PartDesign::Pocket] Pocket169
  BaseFeature = -> Pocket168
  Direction = (-1,-1e-16,-9.4e-15)
  Length = 3
  Length2 = 5
  Profile = -> Sketch181
  ReferenceAxis = -> Sketch181 [N_Axis]
  Refine = true
  Suppressed = false
  Type = 0
FEATURE [Sketcher::SketchObject] Sketch182
  ArcFitTolerance = 1e-06
  AttachmentSupport = -> [Pocket169]
  ExternalGeometry = -> [Pocket169]
  FullyConstrained = true
  MakeInternals = false
  MapMode = 5
  Placement = pos=(0,-52.45,0) rot=(0,0.707107,0.707107;3.14159rad)
  sketch-geometry (4):
    g0: LineSegment StartX=-18.3 StartY=-4 StartZ=0 EndX=-17.3 EndY=-4 EndZ=0
    g1: LineSegment StartX=-17.3 StartY=-4 StartZ=0 EndX=-17.3 EndY=-1.8 EndZ=0
    g2: LineSegment StartX=-17.3 StartY=-1.8 StartZ=0 EndX=-18.3 EndY=-1.8 EndZ=0
    g3: LineSegment StartX=-18.3 StartY=-1.8 StartZ=0 EndX=-18.3 EndY=-4 EndZ=0
  constraints (12):
    c: Coincident(g0,g1)
    c: Coincident(g1,g2)
    c: Coincident(g2,g3)
    c: Coincident(g3,g0)
    c: Horizontal(g0)
    c: Horizontal(g2)
    c: Vertical(g1)
    c: Vertical(g3)
    c: Coincident(g0,g-5)
    c: DistanceY(g-4,g-4) = 3.2
    c: DistanceY(g2,g-4) = 1
    c: DistanceX(g2,g2) = 1
FEATURE [PartDesign::Pocket] Pocket170
  BaseFeature = -> Pocket169
  Direction = (0,-1,2e-16)
  Length = 6
  Length2 = 5
  Profile = -> Sketch182
  ReferenceAxis = -> Sketch182 [N_Axis]
  Refine = true
  Reversed = true
  Suppressed = false
  Type = 0
FEATURE [Sketcher::SketchObject] Sketch183
  ArcFitTolerance = 1e-06
  AttachmentSupport = -> [Pocket170]
  ExternalGeometry = -> [Pocket170]
  FullyConstrained = true
  MakeInternals = false
  MapMode = 5
  Placement = pos=(0,-18.45,0) rot=(1,0,0;1.5708rad)
  sketch-geometry (4):
    g0: LineSegment StartX=18.2 StartY=-4 StartZ=0 EndX=18.2 EndY=-1.8 EndZ=0
    g1: LineSegment StartX=18.2 StartY=-1.8 StartZ=0 EndX=17.2 EndY=-1.8 EndZ=0
    g2: LineSegment StartX=17.2 StartY=-1.8 StartZ=0 EndX=17.2 EndY=-4 EndZ=0
    g3: LineSegment StartX=17.2 StartY=-4 StartZ=0 EndX=18.2 EndY=-4 EndZ=0
  constraints (12):
    c: Coincident(g0,g1)
    c: Coincident(g1,g2)
    c: Coincident(g2,g3)
    c: Coincident(g3,g0)
    c: Vertical(g0)
    c: Vertical(g2)
    c: Horizontal(g1)
    c: Horizontal(g3)
    c: PointOnObject(g0,g-5)
    c: DistanceY(g0,g-4) = 1
    c: PointOnObject(g0,g-4)
    c: DistanceX(g1,g1) = 1
FEATURE [PartDesign::Pocket] Pocket171
  BaseFeature = -> Pocket170
  Direction = (0,1,-2e-16)
  Length = 13
  Length2 = 5
  Profile = -> Sketch183
  ReferenceAxis = -> Sketch183 [N_Axis]
  Refine = true
  Reversed = true
  Suppressed = false
  Type = 0
FEATURE [Sketcher::SketchObject] Sketch184
  ArcFitTolerance = 1e-06
  AttachmentSupport = -> [Pocket171]
  ExternalGeometry = -> [Pocket171]
  FullyConstrained = true
  MakeInternals = false
  MapMode = 5
  Placement = pos=(3.78e-14,0,-4) rot=(1,0,0;3.14159rad)
  sketch-geometry (6):
    g0: LineSegment StartX=8.5 StartY=17.95 StartZ=0 EndX=8.5 EndY=14.05 EndZ=0
    g1: LineSegment StartX=8.5 StartY=14.05 StartZ=0 EndX=13.5 EndY=14.05 EndZ=0
    g2: LineSegment StartX=13.5 StartY=14.05 StartZ=0 EndX=13.5 EndY=17.95 EndZ=0
    g3: ArcOfCircle CenterX=14 CenterY=17.95 CenterZ=0 NormalX=0 NormalY=0 NormalZ=1 AngleXU=0 Radius=0.5 StartAngle=1.5708 EndAngle=3.14159
    g4: ArcOfCircle CenterX=8 CenterY=17.95 CenterZ=0 NormalX=0 NormalY=0 NormalZ=1 AngleXU=0 Radius=0.5 StartAngle=-1.8e-15 EndAngle=1.5708
    g5: LineSegment StartX=8 StartY=18.45 StartZ=0 EndX=14 EndY=18.45 EndZ=0
  constraints (19):
    c: Vertical(g0)
    c: Coincident(g1,g0)
    c: Horizontal(g1)
    c: Coincident(g2,g1)
    c: Vertical(g2)
    c: Coincident(g3,g2)
    c: PointOnObject(g3,g-6)
    c: Coincident(g4,g0)
    c: PointOnObject(g4,g-6)
    c: Tangent(g5,g4) = 1.5708
    c: Coincident(g5,g3)
    c: Radius(g4) = 0.5
    c: Radius(g3) = 0.5
    c: DistanceY(g-4,g1) = 1.5
    c: DistanceX(g1,g-3) = 1.5
    c: DistanceX(g-5,g0) = 1.5
    c: DistanceY(g4,g0) = 0
    c: DistanceY(g2,g3) = 0
    c: DistanceX(g3,g3) = 0
FEATURE [PartDesign::Pocket] Pocket172
  BaseFeature = -> Pocket171
  Direction = (-9.5e-15,0,1)
  Length = 1.7
  Length2 = 5
  Profile = -> Sketch184
  ReferenceAxis = -> Sketch184 [N_Axis]
  Refine = true
  Suppressed = false
  Type = 0
FEATURE [Sketcher::SketchObject] Sketch185
  ArcFitTolerance = 1e-06
  AttachmentSupport = -> [Pocket172]
  ExternalGeometry = -> [Pocket172]
  FullyConstrained = true
  MakeInternals = false
  MapMode = 5
  Placement = pos=(3.78e-14,0,-4) rot=(1,0,0;3.14159rad)
  sketch-geometry (2):
    g0: Circle CenterX=11 CenterY=50.4 CenterZ=0 NormalX=0 NormalY=0 NormalZ=1 AngleXU=0 Radius=2
    g1: Circle CenterX=11 CenterY=26.05 CenterZ=0 NormalX=0 NormalY=0 NormalZ=1 AngleXU=0 Radius=2
  constraints (8):
    c: Radius(g0) = 2
    c: Radius(g1) = 2
    c: DistanceX(g-3,g-3) = 7.2
    c: DistanceX(g-3,g1) = 3.6
    c: DistanceX(g-4,g-4) = 5.8
    c: DistanceX(g-4,g0) = 2.9
    c: DistanceY(g0,g-5) = 4.05
    c: DistanceY(g1,g-6) = 4.3
FEATURE [PartDesign::Pad] Pad136
  BaseFeature = -> Pocket172
  Direction = (9.5e-15,0,-1)
  Length = 1.5
  Length2 = 10
  Profile = -> Sketch185
  ReferenceAxis = -> Sketch185 [N_Axis]
  Refine = true
  Suppressed = false
  Type = 0
FEATURE [Sketcher::SketchObject] Sketch186
  ArcFitTolerance = 1e-06
  AttachmentSupport = -> [Pad136]
  ExternalGeometry = -> [Pad136]
  FullyConstrained = true
  MakeInternals = false
  MapMode = 5
  Placement = pos=(5.21e-14,0,-5.5) rot=(1,0,0;3.14159rad)
  sketch-geometry (2):
    g0: Circle CenterX=11 CenterY=50.4 CenterZ=0 NormalX=0 NormalY=0 NormalZ=1 AngleXU=0 Radius=0.75
    g1: Circle CenterX=11 CenterY=26.05 CenterZ=0 NormalX=0 NormalY=0 NormalZ=1 AngleXU=0 Radius=0.75
  constraints (4):
    c: Coincident(g0,g-3)
    c: Coincident(g1,g-4)
    c: Diameter(g0) = 1.5
    c: Diameter(g1) = 1.5
FEATURE [PartDesign::Pocket] Pocket173
  BaseFeature = -> Pad136
  Direction = (-9.5e-15,0,1)
  Length = 4
  Length2 = 5
  Profile = -> Sketch186
  ReferenceAxis = -> Sketch186 [N_Axis]
  Refine = true
  Suppressed = false
  Type = 0
FEATURE [Sketcher::SketchObject] Sketch299
  ArcFitTolerance = 1e-06
  AttachmentSupport = -> [Pocket173]
  ExternalGeometry = -> [Pocket173]
  FullyConstrained = true
  MakeInternals = false
  MapMode = 5
  Placement = pos=(-9.5e-15,0,1) rot=(0,0,1;0rad)
  sketch-geometry (4):
    g0: LineSegment StartX=2.3 StartY=-16.95 StartZ=0 EndX=2.3 EndY=-30.35 EndZ=0
    g1: LineSegment StartX=2.3 StartY=-30.35 StartZ=0 EndX=19.2 EndY=-30.35 EndZ=0
    g2: LineSegment StartX=19.2 StartY=-30.35 StartZ=0 EndX=19.2 EndY=-16.95 EndZ=0
    g3: LineSegment StartX=19.2 StartY=-16.95 StartZ=0 EndX=2.3 EndY=-16.95 EndZ=0
  constraints (11):
    c: Coincident(g0,g1)
    c: Coincident(g1,g2)
    c: Coincident(g2,g3)
    c: Coincident(g3,g0)
    c: Vertical(g0)
    c: Vertical(g2)
    c: Horizontal(g1)
    c: Horizontal(g3)
    c: PointOnObject(g-3,g1)
    c: Coincident(g2,g-9)
    c: PointOnObject(g-7,g0)
FEATURE [PartDesign::Pocket] Pocket083
  BaseFeature = -> Pocket173
  Direction = (9.5e-15,0,-1)
  Length = 0.2
  Length2 = 5
  Profile = -> Sketch299
  ReferenceAxis = -> Sketch299 [N_Axis]
  Refine = true
  Suppressed = false
  Type = 0
FEATURE [Sketcher::SketchObject] Sketch300
  ArcFitTolerance = 1e-06
  AttachmentSupport = -> [Pocket083]
  ExternalGeometry = -> [Pocket083]
  FullyConstrained = true
  MakeInternals = false
  MapMode = 5
  Placement = pos=(-9.5e-15,0,1) rot=(0,0,1;0rad)
  sketch-geometry (8):
    g0: ArcOfCircle CenterX=3.8 CenterY=-30.85 CenterZ=0 NormalX=0 NormalY=0 NormalZ=1 AngleXU=0 Radius=0.5 StartAngle=7e-16 EndAngle=3.14159
    g1: LineSegment StartX=3.3 StartY=-30.85 StartZ=0 EndX=3.3 EndY=-30.35 EndZ=0
    g2: LineSegment StartX=3.3 StartY=-30.35 StartZ=0 EndX=4.3 EndY=-30.35 EndZ=0
    g3: LineSegment StartX=4.3 StartY=-30.35 StartZ=0 EndX=4.3 EndY=-30.85 EndZ=0
    g4: ArcOfCircle CenterX=18.2 CenterY=-30.85 CenterZ=0 NormalX=0 NormalY=0 NormalZ=1 AngleXU=0 Radius=0.5 StartAngle=1.8e-15 EndAngle=3.14159
    g5: LineSegment StartX=17.7 StartY=-30.85 StartZ=0 EndX=17.7 EndY=-30.35 EndZ=0
    g6: LineSegment StartX=17.7 StartY=-30.35 StartZ=0 EndX=18.7 EndY=-30.35 EndZ=0
    g7: LineSegment StartX=18.7 StartY=-30.35 StartZ=0 EndX=18.7 EndY=-30.85 EndZ=0
  constraints (22):
    c: PointOnObject(g0,g-4)
    c: PointOnObject(g0,g-5)
    c: Coincident(g1,g0)
    c: Coincident(g1,g-4)
    c: Coincident(g2,g1)
    c: Coincident(g2,g-5)
    c: Tangent(g2,g0)
    c: Coincident(g3,g2)
    c: Coincident(g3,g0)
    c: DistanceY(g0,g0) = 0
    c: DistanceY(g0,g0) = 0
    c: PointOnObject(g4,g-7)
    c: PointOnObject(g4,g-8)
    c: DistanceY(g4,g4) = 0
    c: DistanceY(g4,g4) = 0
    c: Coincident(g5,g4)
    c: Coincident(g5,g-7)
    c: Coincident(g6,g5)
    c: Coincident(g6,g-8)
    c: Coincident(g7,g6)
    c: Coincident(g7,g4)
    c: Tangent(g4,g6)
FEATURE [PartDesign::Pocket] Pocket084
  BaseFeature = -> Pocket083
  Direction = (9.5e-15,0,-1)
  Length = 0.2
  Length2 = 5
  Profile = -> Sketch300
  ReferenceAxis = -> Sketch300 [N_Axis]
  Refine = true
  Suppressed = false
  Type = 0
FEATURE [Sketcher::SketchObject] Sketch314
  ArcFitTolerance = 1e-06
  AttachmentSupport = -> [Pocket084]
  ExternalGeometry = -> [Pocket084]
  FullyConstrained = true
  MakeInternals = false
  MapMode = 5
  Placement = pos=(19.8,0,1.873e-13) rot=(0.57735,0.57735,0.57735;2.0944rad)
  sketch-geometry (10):
    g0: ArcOfCircle CenterX=-48.25 CenterY=-4 CenterZ=0 NormalX=0 NormalY=0 NormalZ=1 AngleXU=0 Radius=2.2 StartAngle=1.5708 EndAngle=3.14159
    g1: ArcOfCircle CenterX=-29.35 CenterY=-4 CenterZ=0 NormalX=0 NormalY=0 NormalZ=1 AngleXU=0 Radius=2.2 StartAngle=0 EndAngle=1.5708
    g2: LineSegment StartX=-48.25 StartY=-1.8 StartZ=0 EndX=-29.35 EndY=-1.8 EndZ=0
    g3: ArcOfCircle CenterX=-29.35 CenterY=-4 CenterZ=0 NormalX=0 NormalY=0 NormalZ=1 AngleXU=0 Radius=2 StartAngle=0 EndAngle=1.5708
    g4: LineSegment [constr] StartX=-29.35 StartY=-1.8 StartZ=0 EndX=-29.35 EndY=-2 EndZ=0
    g5: LineSegment StartX=-29.35 StartY=-2 StartZ=0 EndX=-48.25 EndY=-2 EndZ=0
    g6: LineSegment [constr] StartX=-48.25 StartY=-1.8 StartZ=0 EndX=-48.25 EndY=-2 EndZ=0
    g7: ArcOfCircle CenterX=-48.25 CenterY=-4 CenterZ=0 NormalX=0 NormalY=0 NormalZ=1 AngleXU=0 Radius=2 StartAngle=1.5708 EndAngle=3.14159
    g8: LineSegment StartX=-50.25 StartY=-4 StartZ=0 EndX=-50.45 EndY=-4 EndZ=0
    g9: LineSegment StartX=-27.35 StartY=-4 StartZ=0 EndX=-27.15 EndY=-4 EndZ=0
  constraints (26):
    c: Tangent(g0,g-4) = -1.5708
    c: Coincident(g0,g-4)
    c: Tangent(g1,g-5) = -1.5708
    c: Coincident(g1,g-5)
    c: Coincident(g2,g0)
    c: Coincident(g2,g1)
    c: PointOnObject(g3,g-6)
    c: Radius(g3) = 2
    c: PointOnObject(g3,g-6)
    c: Coincident(g4,g1)
    c: Coincident(g4,g3)
    c: Vertical(g4)
    c: Coincident(g5,g3)
    c: Horizontal(g5)
    c: Coincident(g6,g0)
    c: Coincident(g6,g5)
    c: Vertical(g6)
    c: Coincident(g7,g5)
    c: PointOnObject(g7,g-6)
    c: PointOnObject(g7,g-6)
    c: Radius(g7) = 2
    c: Coincident(g8,g7)
    c: Coincident(g8,g0)
    c: Coincident(g9,g3)
    c: Coincident(g9,g1)
    c: DistanceX(g9,g9) = 0.2
FEATURE [PartDesign::Pad] Pad209
  BaseFeature = -> Pocket084
  Direction = (1,1e-16,9.4e-15)
  Length = 1.5
  Length2 = 10
  Profile = -> Sketch314
  ReferenceAxis = -> Sketch314 [N_Axis]
  Refine = true
  Reversed = true
  Suppressed = false
  Type = 0
FEATURE [Sketcher::SketchObject] Sketch315
  ArcFitTolerance = 1e-06
  AttachmentSupport = -> [Pad209]
  ExternalGeometry = -> [Pad209]
  FullyConstrained = true
  MakeInternals = false
  MapMode = 5
  Placement = pos=(2.2,0,2.08e-14) rot=(0.57735,-0.57735,-0.57735;2.0944rad)
  sketch-geometry (8):
    g0: LineSegment StartX=29.35 StartY=-1.8 StartZ=0 EndX=48.25 EndY=-1.8 EndZ=0
    g1: LineSegment StartX=48.25 StartY=-2 StartZ=0 EndX=29.35 EndY=-2 EndZ=0
    g2: ArcOfCircle CenterX=29.35 CenterY=-4 CenterZ=0 NormalX=0 NormalY=0 NormalZ=1 AngleXU=0 Radius=2.2 StartAngle=1.5708 EndAngle=3.14159
    g3: ArcOfCircle CenterX=29.35 CenterY=-4 CenterZ=0 NormalX=0 NormalY=0 NormalZ=1 AngleXU=0 Radius=2 StartAngle=1.5708 EndAngle=3.14159
    g4: LineSegment StartX=27.35 StartY=-4 StartZ=0 EndX=27.15 EndY=-4 EndZ=0
    g5: ArcOfCircle CenterX=48.25 CenterY=-4 CenterZ=0 NormalX=0 NormalY=0 NormalZ=1 AngleXU=0 Radius=2 StartAngle=0 EndAngle=1.5708
    g6: ArcOfCircle CenterX=48.25 CenterY=-4 CenterZ=0 NormalX=0 NormalY=0 NormalZ=1 AngleXU=0 Radius=2.2 StartAngle=-4.29354e-11 EndAngle=1.5708
    g7: LineSegment StartX=50.45 StartY=-4 StartZ=0 EndX=50.25 EndY=-4 EndZ=0
  constraints (16):
    c: Coincident(g1,g-4)
    c: Coincident(g1,g-5)
    c: Coincident(g2,g0)
    c: Tangent(g2,g-6) = -1.5708
    c: Coincident(g3,g1)
    c: Tangent(g3,g-5) = -1.5708
    c: Coincident(g4,g3)
    c: Coincident(g4,g2)
    c: Coincident(g0,g-7)
    c: Coincident(g5,g1)
    c: Tangent(g5,g-3) = -1.5708
    c: Coincident(g6,g0)
    c: Tangent(g6,g-8) = -1.5708
    c: Coincident(g7,g6)
    c: Coincident(g7,g5)
    c: Coincident(g0,g-8)
FEATURE [PartDesign::Pad] Pad210
  BaseFeature = -> Pad209
  Direction = (-1,1e-16,-9.4e-15)
  Length = 1.5
  Length2 = 10
  Profile = -> Sketch315
  ReferenceAxis = -> Sketch315 [N_Axis]
  Refine = true
  Reversed = true
  Suppressed = false
  Type = 0
FEATURE [PartDesign::Body] Body018  label="Rear Legs"
  AllowCompound = false
  Group = -> [Binder019,Sketch171,Pad134,Sketch172,Pocket161,Sketch173,Pocket162,Sketch174,Pocket163,Sketch175,Pocket164,Sketch176,Pad135,Sketch177,Pocket165,Sketch178,Pocket166,Sketch179,Pocket167,Sketch180,Pocket168,Sketch181,Pocket169,Sketch182,Pocket170,Sketch183,Pocket171,Sketch184,Pocket172,Sketch185,Pad136,Sketch186,Pocket173,Sketch299,Pocket083,Sketch300,Pocket084,Sketch314,Pad209,Sketch315,Pad210,+30 more]
  Origin = -> Origin020
  Placement = pos=(33,20.95,0) rot=(0,0,1;0rad)
  Tip = -> Pocket239
COMPONENT P9 — recipe-attached ("Rear Feet", modeled in this document).
Construction recipe (the document's own serialized feature program — sketch geometry with constraints, then the solid features built on it; lengths are millimeters unless a unit is written):

FEATURE [PartDesign::SubShapeBinder] Binder011
  BindCopyOnChange = 0
  BindMode = 2
  ClaimChildren = false
  Context = -> Body019 [Binder011.]
  Fuse = false
  MakeFace = true
  OffsetFill = false
  OffsetIntersection = false
  OffsetJoinType = 0
  OffsetOpenResult = false
  PartialLoad = false
  Refine = true
  Relative = true
  _Version = 2
FEATURE [Sketcher::SketchObject] Sketch188
  ArcFitTolerance = 1e-06
  AttachmentSupport = -> [Binder011]
  ExternalGeometry = -> [Binder011]
  FullyConstrained = true
  MakeInternals = false
  MapMode = 5
  Placement = pos=(2.2,0,2.08e-14) rot=(0.57735,-0.57735,-0.57735;2.0944rad)
  sketch-geometry (10):
    g0: LineSegment StartX=72.35 StartY=-4 StartZ=0 EndX=43.15 EndY=-4 EndZ=0
    g1: LineSegment StartX=43.15 StartY=-4 StartZ=0 EndX=43.15 EndY=1 EndZ=0
    g2: LineSegment StartX=43.15 StartY=1 StartZ=0 EndX=54.45 EndY=1 EndZ=0
    g3: LineSegment StartX=54.45 StartY=1 StartZ=0 EndX=54.45 EndY=3 EndZ=0
    g4: LineSegment StartX=54.45 StartY=3 StartZ=0 EndX=80.05 EndY=3 EndZ=0
    g5: LineSegment StartX=80.05 StartY=3 StartZ=0 EndX=80.05 EndY=-4 EndZ=0
    g6: LineSegment StartX=80.05 StartY=-4 StartZ=0 EndX=77.35 EndY=-4 EndZ=0
    g7: LineSegment StartX=77.35 StartY=-4 StartZ=0 EndX=77.35 EndY=0.1 EndZ=0
    g8: LineSegment StartX=77.35 StartY=0.1 StartZ=0 EndX=72.35 EndY=0.1 EndZ=0
    g9: LineSegment StartX=72.35 StartY=0.1 StartZ=0 EndX=72.35 EndY=-4 EndZ=0
  constraints (31):
    c: Horizontal(g0)
    c: Coincident(g1,g0)
    c: Vertical(g1)
    c: Coincident(g2,g1)
    c: Horizontal(g2)
    c: Coincident(g3,g2)
    c: Vertical(g3)
    c: Coincident(g4,g3)
    c: Horizontal(g4)
    c: Vertical(g5)
    c: Coincident(g6,g5)
    c: Horizontal(g6)
    c: Coincident(g7,g6)
    c: Vertical(g7)
    c: Coincident(g8,g7)
    c: Horizontal(g8)
    c: Vertical(g9)
    c: DistanceY(g1,g1) = 5
    c: DistanceX(g2,g2) = 11.3
    c: DistanceX(g4,g4) = 25.6
    c: DistanceY(g-4,g-4) = 4.8
    c: PointOnObject(g-5,g0)
    c: DistanceX(g2,g-4) = 0
    c: DistanceY(g3,g3) = 2
    c: Coincident(g5,g4)
    c: Coincident(g9,g0)
    c: DistanceY(g5,g5) = 7
    c: DistanceX(g8,g8) = 5
    c: DistanceY(g9,g9) = 4.1
    c: Coincident(g9,g8)
    c: DistanceX(g6,g6) = 2.7
FEATURE [PartDesign::Pad] Pad138
  Direction = (-1,1e-16,-9.4e-15)
  Length = 2
  Length2 = 10
  Profile = -> Sketch188
  ReferenceAxis = -> Sketch188 [N_Axis]
  Refine = true
  Suppressed = false
  Type = 0
FEATURE [Sketcher::SketchObject] Sketch189
  ArcFitTolerance = 1e-06
  AttachmentSupport = -> [Pad138]
  ExternalGeometry = -> [Pad138]
  FullyConstrained = true
  MakeInternals = false
  MapMode = 5
  Placement = pos=(-2.83e-14,3e-16,3) rot=(0,0,1;0rad)
  sketch-geometry (4):
    g0: LineSegment StartX=2.2 StartY=-54.45 StartZ=0 EndX=2.2 EndY=-80.05 EndZ=0
    g1: LineSegment StartX=2.2 StartY=-80.05 StartZ=0 EndX=19.8 EndY=-80.05 EndZ=0
    g2: LineSegment StartX=19.8 StartY=-80.05 StartZ=0 EndX=19.8 EndY=-54.45 EndZ=0
    g3: LineSegment StartX=19.8 StartY=-54.45 StartZ=0 EndX=2.2 EndY=-54.45 EndZ=0
  constraints (10):
    c: Coincident(g0,g1)
    c: Coincident(g1,g2)
    c: Coincident(g2,g3)
    c: Coincident(g3,g0)
    c: Vertical(g2)
    c: Horizontal(g1)
    c: Horizontal(g3)
    c: Coincident(g0,g-3)
    c: DistanceX(g1,g1) = 17.6
    c: Coincident(g0,g-5)
FEATURE [PartDesign::Pad] Pad139
  BaseFeature = -> Pad138
  Direction = (-9.4e-15,0,1)
  Length = 2
  Length2 = 10
  Profile = -> Sketch189
  ReferenceAxis = -> Sketch189 [N_Axis]
  Refine = true
  Reversed = true
  Suppressed = false
  Type = 0
FEATURE [Sketcher::SketchObject] Sketch190
  ArcFitTolerance = 1e-06
  AttachmentSupport = -> [Pad139]
  ExternalGeometry = -> [Pad139]
  FullyConstrained = true
  MakeInternals = false
  MapMode = 5
  Placement = pos=(19.8,0,1.869e-13) rot=(0.57735,0.57735,0.57735;2.0944rad)
  sketch-geometry (10):
    g0: LineSegment StartX=-80.05 StartY=-4 StartZ=0 EndX=-80.05 EndY=3 EndZ=0
    g1: LineSegment StartX=-80.05 StartY=3 StartZ=0 EndX=-54.45 EndY=3 EndZ=0
    g2: LineSegment StartX=-54.45 StartY=3 StartZ=0 EndX=-54.45 EndY=1 EndZ=0
    g3: LineSegment StartX=-54.45 StartY=1 StartZ=0 EndX=-43.15 EndY=1 EndZ=0
    g4: LineSegment StartX=-43.15 StartY=1 StartZ=0 EndX=-43.15 EndY=-4 EndZ=0
    g5: LineSegment StartX=-43.15 StartY=-4 StartZ=0 EndX=-72.35 EndY=-4 EndZ=0
    g6: LineSegment StartX=-72.35 StartY=-4 StartZ=0 EndX=-72.35 EndY=0.1 EndZ=0
    g7: LineSegment StartX=-72.35 StartY=0.1 StartZ=0 EndX=-77.35 EndY=0.1 EndZ=0
    g8: LineSegment StartX=-77.35 StartY=0.1 StartZ=0 EndX=-77.35 EndY=-4 EndZ=0
    g9: LineSegment StartX=-77.35 StartY=-4 StartZ=0 EndX=-80.05 EndY=-4 EndZ=0
  constraints (20):
    c: Coincident(g0,g-13)
    c: Coincident(g0,g-4)
    c: Coincident(g1,g0)
    c: Coincident(g1,g-5)
    c: Coincident(g2,g1)
    c: Coincident(g2,g-7)
    c: Coincident(g3,g2)
    c: Coincident(g3,g-7)
    c: Coincident(g4,g3)
    c: Coincident(g4,g-8)
    c: Coincident(g5,g4)
    c: Coincident(g5,g-9)
    c: Coincident(g6,g5)
    c: Coincident(g6,g-10)
    c: Coincident(g7,g6)
    c: Coincident(g7,g-11)
    c: Coincident(g8,g7)
    c: Coincident(g8,g-12)
    c: Coincident(g9,g8)
    c: Coincident(g9,g0)
FEATURE [PartDesign::Pad] Pad140
  BaseFeature = -> Pad139
  Direction = (1,0,9.3e-15)
  Length = 2
  Length2 = 10
  Profile = -> Sketch190
  ReferenceAxis = -> Sketch190 [N_Axis]
  Refine = true
  Suppressed = false
  Type = 0
FEATURE [Sketcher::SketchObject] Sketch191
  ArcFitTolerance = 1e-06
  AttachmentSupport = -> [Pad140]
  ExternalGeometry = -> [Pad140]
  FullyConstrained = true
  MakeInternals = false
  MapMode = 5
  Placement = pos=(2.88e-14,-80.05,-5.28e-14) rot=(1,0,0;1.5708rad)
  sketch-geometry (6):
    g0: LineSegment StartX=2.2 StartY=1 StartZ=0 EndX=2.2 EndY=-4 EndZ=0
    g1: LineSegment StartX=2.2 StartY=-4 StartZ=0 EndX=7.55 EndY=-4 EndZ=0
    g2: LineSegment StartX=2.2 StartY=1 StartZ=0 EndX=19.8 EndY=1 EndZ=0
    g3: LineSegment StartX=19.8 StartY=1 StartZ=0 EndX=19.8 EndY=-4 EndZ=0
    g4: LineSegment StartX=19.8 StartY=-4 StartZ=0 EndX=14.45 EndY=-4 EndZ=0
    g5: ArcOfCircle CenterX=11 CenterY=-4 CenterZ=0 NormalX=0 NormalY=0 NormalZ=1 AngleXU=0 Radius=3.45 StartAngle=3.14159 EndAngle=6.28319
  constraints (15):
    c: Coincident(g0,g-4)
    c: Coincident(g0,g-4)
    c: Coincident(g1,g0)
    c: Horizontal(g1)
    c: Coincident(g2,g0)
    c: Coincident(g2,g-5)
    c: Coincident(g3,g2)
    c: Coincident(g3,g-5)
    c: Coincident(g4,g3)
    c: Horizontal(g4)
    c: Coincident(g5,g1)
    c: Coincident(g5,g4)
    c: Diameter(g5) = 6.9
    c: DistanceY(g4,g5) = 0
    c: DistanceX(g0,g5) = 8.8
FEATURE [PartDesign::Pad] Pad141
  BaseFeature = -> Pad140
  Direction = (0,-1,2e-16)
  Length = 4
  Length2 = 10
  Profile = -> Sketch191
  ReferenceAxis = -> Sketch191 [N_Axis]
  Refine = true
  Reversed = true
  Suppressed = false
  Type = 0
FEATURE [PartDesign::Fillet] Fillet006
  Base = -> Pad141 [Edge30,Edge25]
  BaseFeature = -> Pad141
  Radius = 1.1
  Refine = true
  SupportTransform = false
  Suppressed = false
  UseAllEdges = false
FEATURE [Sketcher::SketchObject] Sketch192
  ArcFitTolerance = 1e-06
  AttachmentSupport = -> [Fillet006]
  ExternalGeometry = -> [Fillet006]
  FullyConstrained = true
  MakeInternals = false
  MapMode = 5
  Placement = pos=(2.16e-14,-80.05,3.066e-13) rot=(1,0,0;1.5708rad)
  sketch-geometry (4):
    g0: ArcOfCircle CenterX=11 CenterY=-4 CenterZ=0 NormalX=0 NormalY=0 NormalZ=1 AngleXU=0 Radius=2 StartAngle=3.14159 EndAngle=6.28319
    g1: LineSegment StartX=9 StartY=-4 StartZ=0 EndX=9 EndY=3 EndZ=0
    g2: LineSegment StartX=13 StartY=-4 StartZ=0 EndX=13 EndY=3 EndZ=0
    g3: LineSegment StartX=13 StartY=3 StartZ=0 EndX=9 EndY=3 EndZ=0
  constraints (13):
    c: Coincident(g1,g0)
    c: PointOnObject(g1,g-4)
    c: Vertical(g1)
    c: Coincident(g2,g0)
    c: PointOnObject(g2,g-4)
    c: Vertical(g2)
    c: Coincident(g3,g2)
    c: Coincident(g3,g1)
    c: Coincident(g0,g-3)
    c: DistanceY(g0,g0) = 0
    c: DistanceY(g0,g0) = 0
    c: Diameter(g-3) = 6.9
    c: Diameter(g0) = 4
FEATURE [PartDesign::Pocket] Pocket141
  BaseFeature = -> Fillet006
  Direction = (0,1,-4e-15)
  Length = 5.1
  Length2 = 5
  Profile = -> Sketch192
  ReferenceAxis = -> Sketch192 [N_Axis]
  Refine = true
  Suppressed = false
  Type = 0
FEATURE [Sketcher::SketchObject] Sketch193
  ArcFitTolerance = 1e-06
  AttachmentSupport = -> [Pocket141]
  ExternalGeometry = -> [Pocket141]
  FullyConstrained = true
  MakeInternals = false
  MapMode = 5
  Placement = pos=(2.16e-14,-80.05,3.066e-13) rot=(1,0,0;1.5708rad)
  sketch-geometry (8):
    g0: LineSegment StartX=21.8 StartY=3 StartZ=0 EndX=17.8 EndY=3 EndZ=0
    g1: LineSegment StartX=17.8 StartY=3 StartZ=0 EndX=17.8 EndY=-0.5 EndZ=0
    g2: LineSegment StartX=17.8 StartY=-0.5 StartZ=0 EndX=21.8 EndY=-0.5 EndZ=0
    g3: LineSegment StartX=21.8 StartY=-0.5 StartZ=0 EndX=21.8 EndY=3 EndZ=0
    g4: LineSegment StartX=0.2 StartY=3 StartZ=0 EndX=0.2 EndY=-0.5 EndZ=0
    g5: LineSegment StartX=0.2 StartY=-0.5 StartZ=0 EndX=4.2 EndY=-0.5 EndZ=0
    g6: LineSegment StartX=4.2 StartY=-0.5 StartZ=0 EndX=4.2 EndY=3 EndZ=0
    g7: LineSegment StartX=4.2 StartY=3 StartZ=0 EndX=0.2 EndY=3 EndZ=0
  constraints (22):
    c: Coincident(g0,g1)
    c: Coincident(g1,g2)
    c: Coincident(g2,g3)
    c: Coincident(g3,g0)
    c: Horizontal(g0)
    c: Horizontal(g2)
    c: Vertical(g1)
    c: Vertical(g3)
    c: Coincident(g0,g-6)
    c: Coincident(g4,g5)
    c: Coincident(g5,g6)
    c: Coincident(g6,g7)
    c: Coincident(g7,g4)
    c: Vertical(g4)
    c: Vertical(g6)
    c: Horizontal(g5)
    c: Horizontal(g7)
    c: Coincident(g4,g-4)
    c: DistanceX(g5,g5) = 4
    c: DistanceX(g2,g2) = 4
    c: DistanceY(g1,g1) = 3.5
    c: DistanceY(g6,g6) = 3.5
FEATURE [PartDesign::Pocket] Pocket142
  BaseFeature = -> Pocket141
  Direction = (0,1,-4e-15)
  Length = 2.1
  Length2 = 5
  Profile = -> Sketch193
  ReferenceAxis = -> Sketch193 [N_Axis]
  Refine = true
  Suppressed = false
  Type = 0
FEATURE [PartDesign::Fillet] Fillet007
  Base = -> Pocket142 [Edge81,Edge79,Edge83,Edge29]
  BaseFeature = -> Pocket142
  Radius = 1
  Refine = true
  SupportTransform = false
  Suppressed = false
  UseAllEdges = false
FEATURE [Sketcher::SketchObject] Sketch194
  ArcFitTolerance = 1e-06
  AttachmentSupport = -> [Fillet007]
  ExternalGeometry = -> [Fillet007]
  FullyConstrained = true
  MakeInternals = false
  MapMode = 5
  Placement = pos=(-2.45e-14,0,3) rot=(0,0,1;0rad)
  sketch-geometry (12):
    g0: LineSegment StartX=2.2 StartY=-62.85 StartZ=0 EndX=2.2 EndY=-68.85 EndZ=0
    g1: LineSegment StartX=3.2 StartY=-69.85 StartZ=0 EndX=18.8 EndY=-69.85 EndZ=0
    g2: LineSegment StartX=19.8 StartY=-68.85 StartZ=0 EndX=19.8 EndY=-62.85 EndZ=0
    g3: LineSegment StartX=18.8 StartY=-61.85 StartZ=0 EndX=3.2 EndY=-61.85 EndZ=0
    g4: ArcOfCircle CenterX=3.2 CenterY=-68.85 CenterZ=0 NormalX=0 NormalY=0 NormalZ=1 AngleXU=0 Radius=1 StartAngle=3.14159 EndAngle=4.71239
    g5: GeomPoint [constr] X=2.2 Y=-69.85 Z=0
    g6: ArcOfCircle CenterX=18.8 CenterY=-68.85 CenterZ=0 NormalX=0 NormalY=0 NormalZ=1 AngleXU=0 Radius=1 StartAngle=4.71239 EndAngle=6.28319
    g7: GeomPoint [constr] X=19.8 Y=-69.85 Z=0
    g8: ArcOfCircle CenterX=18.8 CenterY=-62.85 CenterZ=0 NormalX=0 NormalY=0 NormalZ=1 AngleXU=0 Radius=1 StartAngle=-2.7e-15 EndAngle=1.5708
    g9: GeomPoint [constr] X=19.8 Y=-61.85 Z=0
    g10: ArcOfCircle CenterX=3.2 CenterY=-62.85 CenterZ=0 NormalX=0 NormalY=0 NormalZ=1 AngleXU=0 Radius=1 StartAngle=1.5708 EndAngle=3.14159
    g11: GeomPoint [constr] X=2.2 Y=-61.85 Z=0
  constraints (28):
    c: Vertical(g0)
    c: Vertical(g2)
    c: Horizontal(g1)
    c: Horizontal(g3)
    c: PointOnObject(g5,g0)
    c: PointOnObject(g5,g1)
    c: Tangent(g0,g4) = -1.5708
    c: Tangent(g1,g4) = -1.5708
    c: PointOnObject(g7,g1)
    c: PointOnObject(g7,g2)
    c: Tangent(g1,g6) = -1.5708
    c: Tangent(g2,g6) = -1.5708
    c: PointOnObject(g9,g2)
    c: PointOnObject(g9,g3)
    c: Tangent(g2,g8) = -1.5708
    c: Tangent(g3,g8) = -1.5708
    c: PointOnObject(g11,g0)
    c: PointOnObject(g11,g3)
    c: Tangent(g0,g10) = -1.5708
    c: Tangent(g3,g10) = -1.5708
    c: Radius(g10) = 1
    c: Radius(g8) = 1
    c: Radius(g6) = 1
    c: Radius(g4) = 1
    c: DistanceY(g-3,g1) = 10.2
    c: DistanceX(g-5,g0) = 2
    c: DistanceX(g2,g-4) = 2
    c: DistanceY(g1,g3) = 8
FEATURE [PartDesign::Pad] Pad142
  BaseFeature = -> Fillet007
  Direction = (-8.1e-15,0,1)
  Length = 0.5
  Length2 = 10
  Profile = -> Sketch194
  ReferenceAxis = -> Sketch194 [N_Axis]
  Refine = true
  Suppressed = false
  Type = 0
FEATURE [Sketcher::SketchObject] Sketch195
  ArcFitTolerance = 1e-06
  AttachmentSupport = -> [Pad142]
  ExternalGeometry = -> [Pad142]
  FullyConstrained = true
  MakeInternals = false
  MapMode = 5
  Placement = pos=(0.2,0,1.9e-15) rot=(0.57735,-0.57735,-0.57735;2.0944rad)
  sketch-geometry (5):
    g0: LineSegment StartX=54.45 StartY=1 StartZ=0 EndX=56.45 EndY=-4 EndZ=0
    g1: LineSegment StartX=56.45 StartY=-4 StartZ=0 EndX=59.45 EndY=-4 EndZ=0
    g2: LineSegment StartX=59.45 StartY=-4 StartZ=0 EndX=59.45 EndY=3 EndZ=0
    g3: LineSegment StartX=59.45 StartY=3 StartZ=0 EndX=54.45 EndY=3 EndZ=0
    g4: LineSegment StartX=54.45 StartY=3 StartZ=0 EndX=54.45 EndY=1 EndZ=0
  constraints (13):
    c: Coincident(g0,g-3)
    c: PointOnObject(g0,g-5)
    c: Coincident(g1,g0)
    c: PointOnObject(g1,g-5)
    c: Coincident(g2,g1)
    c: PointOnObject(g2,g-4)
    c: Vertical(g2)
    c: Coincident(g3,g2)
    c: Coincident(g3,g-4)
    c: Coincident(g4,g3)
    c: Coincident(g4,g0)
    c: DistanceX(g3,g3) = 5
    c: DistanceX(g1,g1) = 3
FEATURE [PartDesign::Pocket] Pocket143
  BaseFeature = -> Pad142
  Direction = (1,0,9.3e-15)
  Length = 0.75
  Length2 = 5
  Profile = -> Sketch195
  ReferenceAxis = -> Sketch195 [N_Axis]
  Refine = true
  Suppressed = false
  Type = 0
FEATURE [PartDesign::Fillet] Fillet008
  Base = -> Pocket143 [Edge128,Edge5]
  BaseFeature = -> Pocket143
  Radius = 0.5
  Refine = true
  SupportTransform = false
  Suppressed = false
  UseAllEdges = false
FEATURE [Sketcher::SketchObject] Sketch196
  ArcFitTolerance = 1e-06
  AttachmentSupport = -> [Fillet008]
  ExternalGeometry = -> [Fillet008]
  FullyConstrained = true
  MakeInternals = false
  MapMode = 5
  Placement = pos=(21.8,0,2.102e-13) rot=(0.57735,0.57735,0.57735;2.0944rad)
  sketch-geometry (5):
    g0: LineSegment StartX=-54.45 StartY=1 StartZ=0 EndX=-56.45 EndY=-4 EndZ=0
    g1: LineSegment StartX=-56.45 StartY=-4 StartZ=0 EndX=-59.45 EndY=-4 EndZ=0
    g2: LineSegment StartX=-59.45 StartY=-4 StartZ=0 EndX=-59.45 EndY=3 EndZ=0
    g3: LineSegment StartX=-59.45 StartY=3 StartZ=0 EndX=-54.45 EndY=3 EndZ=0
    g4: LineSegment StartX=-54.45 StartY=3 StartZ=0 EndX=-54.45 EndY=1 EndZ=0
  constraints (13):
    c: Coincident(g0,g-4)
    c: PointOnObject(g0,g-6)
    c: Coincident(g1,g0)
    c: PointOnObject(g1,g-6)
    c: Coincident(g2,g1)
    c: PointOnObject(g2,g-5)
    c: Vertical(g2)
    c: Coincident(g3,g2)
    c: Coincident(g3,g-5)
    c: Coincident(g4,g3)
    c: Coincident(g4,g0)
    c: DistanceX(g1,g1) = 3
    c: DistanceX(g3,g3) = 5
FEATURE [PartDesign::Pocket] Pocket144
  BaseFeature = -> Fillet008
  Direction = (-1,-1e-16,-9.4e-15)
  Length = 0.75
  Length2 = 5
  Profile = -> Sketch196
  ReferenceAxis = -> Sketch196 [N_Axis]
  Refine = true
  Suppressed = false
  Type = 0
FEATURE [PartDesign::Fillet] Fillet009
  Base = -> Pocket144 [Edge81,Edge159]
  BaseFeature = -> Pocket144
  Radius = 0.5
  Refine = true
  SupportTransform = false
  Suppressed = false
  UseAllEdges = false
FEATURE [Sketcher::SketchObject] Sketch197
  ArcFitTolerance = 1e-06
  AttachmentSupport = -> [Fillet009]
  ExternalGeometry = -> [Fillet009]
  FullyConstrained = true
  MakeInternals = false
  MapMode = 5
  Placement = pos=(0.2,0,1.9e-15) rot=(0.57735,-0.57735,-0.57735;2.0944rad)
  sketch-geometry (4):
    g0: LineSegment StartX=43.15 StartY=1 StartZ=0 EndX=43.15 EndY=-4 EndZ=0
    g1: LineSegment StartX=43.15 StartY=-4 StartZ=0 EndX=50.15 EndY=-4 EndZ=0
    g2: LineSegment StartX=50.15 StartY=-4 StartZ=0 EndX=50.15 EndY=1 EndZ=0
    g3: LineSegment StartX=50.15 StartY=1 StartZ=0 EndX=43.15 EndY=1 EndZ=0
  constraints (11):
    c: Coincident(g0,g1)
    c: Coincident(g1,g2)
    c: Coincident(g2,g3)
    c: Coincident(g3,g0)
    c: Vertical(g0)
    c: Vertical(g2)
    c: Horizontal(g1)
    c: Horizontal(g3)
    c: Coincident(g0,g-3)
    c: PointOnObject(g1,g-4)
    c: DistanceX(g3,g3) = 7
FEATURE [PartDesign::Pad] Pad143
  BaseFeature = -> Fillet009
  Direction = (-1,0,-9.3e-15)
  Length = 5
  Length2 = 10
  Profile = -> Sketch197
  ReferenceAxis = -> Sketch197 [N_Axis]
  Refine = true
  Suppressed = false
  Type = 0
FEATURE [Sketcher::SketchObject] Sketch198
  ArcFitTolerance = 1e-06
  AttachmentSupport = -> [Pad143]
  ExternalGeometry = -> [Pad143]
  FullyConstrained = true
  MakeInternals = false
  MapMode = 5
  Placement = pos=(21.8,0,2.102e-13) rot=(0.57735,0.57735,0.57735;2.0944rad)
  sketch-geometry (4):
    g0: LineSegment StartX=-43.15 StartY=1 StartZ=0 EndX=-50.15 EndY=1 EndZ=0
    g1: LineSegment StartX=-50.15 StartY=1 StartZ=0 EndX=-50.15 EndY=-4 EndZ=0
    g2: LineSegment StartX=-50.15 StartY=-4 StartZ=0 EndX=-43.15 EndY=-4 EndZ=0
    g3: LineSegment StartX=-43.15 StartY=-4 StartZ=0 EndX=-43.15 EndY=1 EndZ=0
  constraints (11):
    c: Coincident(g0,g1)
    c: Coincident(g1,g2)
    c: Coincident(g2,g3)
    c: Coincident(g3,g0)
    c: Horizontal(g0)
    c: Horizontal(g2)
    c: Vertical(g1)
    c: Vertical(g3)
    c: Coincident(g0,g-3)
    c: PointOnObject(g1,g-4)
    c: DistanceX(g0,g0) = 7
FEATURE [PartDesign::Pad] Pad144
  BaseFeature = -> Pad143
  Direction = (1,1e-16,9.4e-15)
  Length = 5
  Length2 = 10
  Profile = -> Sketch198
  ReferenceAxis = -> Sketch198 [N_Axis]
  Refine = true
  Suppressed = false
  Type = 0
FEATURE [PartDesign::Fillet] Fillet010
  Base = -> Pad144 [Edge189,Edge192,Edge183,Edge182]
  BaseFeature = -> Pad144
  Radius = 0.5
  Refine = true
  SupportTransform = false
  Suppressed = false
  UseAllEdges = false
FEATURE [Sketcher::SketchObject] Sketch199
  ArcFitTolerance = 1e-06
  AttachmentSupport = -> [Fillet010]
  ExternalGeometry = -> [Fillet010]
  FullyConstrained = true
  MakeInternals = false
  MapMode = 5
  Placement = pos=(-1.46e-14,6e-16,1) rot=(0,0,1;0rad)
  sketch-geometry (2):
    g0: Circle CenterX=-1.3 CenterY=-46.65 CenterZ=0 NormalX=0 NormalY=0 NormalZ=1 AngleXU=0 Radius=2
    g1: Circle CenterX=23.3 CenterY=-46.65 CenterZ=0 NormalX=0 NormalY=0 NormalZ=1 AngleXU=0 Radius=2
  constraints (8):
    c: Diameter(g0) = 4
    c: Diameter(g1) = 4
    c: DistanceX(g-6,g-4) = 7
    c: DistanceY(g-5,g-3) = 7
    c: DistanceX(g-6,g0) = 3.5
    c: DistanceX(g1,g-9) = 3.5
    c: DistanceY(g1,g-7) = 3.5
    c: DistanceY(g0,g-3) = 3.5
FEATURE [PartDesign::Pocket] Pocket145
  BaseFeature = -> Fillet010
  Direction = (1.46e-14,0,-1)
  Length = 2
  Length2 = 5
  Profile = -> Sketch199
  ReferenceAxis = -> Sketch199 [N_Axis]
  Refine = true
  Suppressed = false
  Type = 0
FEATURE [Sketcher::SketchObject] Sketch200
  ArcFitTolerance = 1e-06
  AttachmentSupport = -> [Pocket145]
  ExternalGeometry = -> [Pocket145]
  FullyConstrained = true
  MakeInternals = false
  MapMode = 5
  Placement = pos=(3.74e-14,0,-4) rot=(1,0,0;3.14159rad)
  sketch-geometry (2):
    g0: Circle CenterX=-1.3 CenterY=46.65 CenterZ=0 NormalX=0 NormalY=0 NormalZ=1 AngleXU=0 Radius=2
    g1: Circle CenterX=23.3 CenterY=46.65 CenterZ=0 NormalX=0 NormalY=0 NormalZ=1 AngleXU=0 Radius=2
  constraints (8):
    c: Diameter(g0) = 4
    c: Diameter(g1) = 4
    c: DistanceX(g-8,g-10) = 7
    c: DistanceX(g-9,g-7) = 0
    c: DistanceX(g-8,g0) = 3.5
    c: DistanceX(g1,g-4) = 3.5
    c: DistanceY(g1,g-3) = 3.5
    c: DistanceY(g0,g-7) = 3.5
FEATURE [PartDesign::Pocket] Pocket146
  BaseFeature = -> Pocket145
  Direction = (-9.4e-15,0,1)
  Length = 2.2
  Length2 = 5
  Profile = -> Sketch200
  ReferenceAxis = -> Sketch200 [N_Axis]
  Refine = true
  Suppressed = false
  Type = 0
FEATURE [Sketcher::SketchObject] Sketch201
  ArcFitTolerance = 1e-06
  AttachmentSupport = -> [Pocket146]
  ExternalGeometry = -> [Pocket146]
  FullyConstrained = true
  MakeInternals = false
  MapMode = 5
  Placement = pos=(1.46e-14,0,-1) rot=(0,0,1;0rad)
  sketch-geometry (2):
    g0: Circle CenterX=-1.3 CenterY=-46.65 CenterZ=0 NormalX=0 NormalY=0 NormalZ=1 AngleXU=0 Radius=1
    g1: Circle CenterX=23.3 CenterY=-46.65 CenterZ=0 NormalX=0 NormalY=0 NormalZ=1 AngleXU=0 Radius=1
  constraints (4):
    c: Coincident(g0,g-4)
    c: Coincident(g1,g-3)
    c: Diameter(g0) = 2
    c: Diameter(g1) = 2
FEATURE [PartDesign::Pocket] Pocket147
  BaseFeature = -> Pocket146
  Direction = (1.46e-14,0,-1)
  Length = 5
  Length2 = 5
  Profile = -> Sketch201
  ReferenceAxis = -> Sketch201 [N_Axis]
  Refine = true
  Suppressed = false
  Type = 0
FEATURE [Sketcher::SketchObject] Sketch202
  ArcFitTolerance = 1e-06
  AttachmentSupport = -> [Pocket147]
  ExternalGeometry = -> [Pocket147]
  FullyConstrained = true
  MakeInternals = false
  MapMode = 5
  Placement = pos=(2.2,0,2.07e-14) rot=(0.57735,0.57735,0.57735;2.0944rad)
  sketch-geometry (1):
    g0: Circle CenterX=-48.15 CenterY=-4 CenterZ=0 NormalX=0 NormalY=0 NormalZ=1 AngleXU=0 Radius=2
  constraints (4):
    c: Diameter(g0) = 4
    c: DistanceY(g-4,g-4) = 5
    c: DistanceY(g-5,g0) = 0
    c: DistanceX(g0,g-5) = 5
FEATURE [PartDesign::Pad] Pad145
  BaseFeature = -> Pocket147
  Direction = (1,0,9.3e-15)
  Length = 2
  Length2 = 10
  Profile = -> Sketch202
  ReferenceAxis = -> Sketch202 [N_Axis]
  Refine = true
  Suppressed = false
  Type = 0
FEATURE [Sketcher::SketchObject] Sketch203
  ArcFitTolerance = 1e-06
  AttachmentSupport = -> [Pad145]
  ExternalGeometry = -> [Pad145]
  FullyConstrained = true
  MakeInternals = false
  MapMode = 5
  Placement = pos=(4.2,0,3.88e-14) rot=(0.57735,0.57735,0.57735;2.0944rad)
  sketch-geometry (1):
    g0: Circle CenterX=-48.15 CenterY=-4 CenterZ=0 NormalX=0 NormalY=0 NormalZ=1 AngleXU=0 Radius=3
  constraints (2):
    c: Coincident(g0,g-3)
    c: Diameter(g0) = 6
FEATURE [PartDesign::Pad] Pad146
  BaseFeature = -> Pad145
  Direction = (1,0,9.3e-15)
  Length = 2
  Length2 = 10
  Profile = -> Sketch203
  ReferenceAxis = -> Sketch203 [N_Axis]
  Refine = true
  Suppressed = false
  Type = 0
FEATURE [Sketcher::SketchObject] Sketch204
  ArcFitTolerance = 1e-06
  AttachmentSupport = -> [Pad146]
  ExternalGeometry = -> [Pad146]
  FullyConstrained = true
  MakeInternals = false
  MapMode = 5
  Placement = pos=(19.8,0,1.909e-13) rot=(0.57735,-0.57735,-0.57735;2.0944rad)
  sketch-geometry (1):
    g0: Circle CenterX=48.15 CenterY=-4 CenterZ=0 NormalX=0 NormalY=0 NormalZ=1 AngleXU=0 Radius=2
  constraints (3):
    c: PointOnObject(g0,g-3)
    c: Radius(g0) = 2
    c: DistanceX(g-4,g0) = 5
FEATURE [PartDesign::Pad] Pad147
  BaseFeature = -> Pad146
  Direction = (-1,1e-16,-9.4e-15)
  Length = 2
  Length2 = 10
  Profile = -> Sketch204
  ReferenceAxis = -> Sketch204 [N_Axis]
  Refine = true
  Suppressed = false
  Type = 0
FEATURE [Sketcher::SketchObject] Sketch205
  ArcFitTolerance = 1e-06
  AttachmentSupport = -> [Pad147]
  ExternalGeometry = -> [Pad147]
  FullyConstrained = true
  MakeInternals = false
  MapMode = 5
  Placement = pos=(17.8,-1.05e-14,1.643e-13) rot=(0.57735,-0.57735,-0.57735;2.0944rad)
  sketch-geometry (1):
    g0: Circle CenterX=48.15 CenterY=-4 CenterZ=0 NormalX=0 NormalY=0 NormalZ=1 AngleXU=0 Radius=3
  constraints (2):
    c: Coincident(g0,g-3)
    c: Diameter(g0) = 6
FEATURE [PartDesign::Pad] Pad148
  BaseFeature = -> Pad147
  Direction = (-1,0,-9.3e-15)
  Length = 2
  Length2 = 10
  Profile = -> Sketch205
  ReferenceAxis = -> Sketch205 [N_Axis]
  Refine = true
  Suppressed = false
  Type = 0
FEATURE [PartDesign::Fillet] Fillet011
  Base = -> Pad148 [Edge14,Edge148]
  BaseFeature = -> Pad148
  Radius = 0.5
  Refine = true
  SupportTransform = false
  Suppressed = false
  UseAllEdges = false
FEATURE [PartDesign::Body] Body019  label="Rear Feet"
  AllowCompound = false
  Group = -> [Binder011,Sketch188,Pad138,Sketch189,Pad139,Sketch190,Pad140,Sketch191,Pad141,Fillet006,Sketch192,Pocket141,Sketch193,Pocket142,Fillet007,Sketch194,Pad142,Sketch195,Pocket143,Fillet008,Sketch196,Pocket144,Fillet009,Sketch197,Pad143,Sketch198,Pad144,Fillet010,Sketch199,Pocket145,Sketch200,Pocket146,Sketch201,Pocket147,Sketch202,Pad145,Sketch203,Pad146,Sketch204,Pad147,Sketch205,Pad148,Fillet011]
  Origin = -> Origin021
  Placement = pos=(33,38,0) rot=(0,0,1;0rad)
  Tip = -> Fillet011
COMPONENT P10 — recipe-attached ("Front Feet", modeled in this document).
Construction recipe (the document's own serialized feature program — sketch geometry with constraints, then the solid features built on it; lengths are millimeters unless a unit is written):

FEATURE [PartDesign::SubShapeBinder] Binder012
  BindCopyOnChange = 0
  BindMode = 2
  ClaimChildren = false
  Context = -> Body020 [Binder012.]
  Fuse = false
  MakeFace = true
  OffsetFill = false
  OffsetIntersection = false
  OffsetJoinType = 0
  OffsetOpenResult = false
  PartialLoad = false
  Refine = true
  Relative = true
  _Version = 2
FEATURE [Sketcher::SketchObject] Sketch206
  ArcFitTolerance = 1e-06
  AttachmentSupport = -> [Binder012]
  ExternalGeometry = -> [Binder012]
  FullyConstrained = true
  MakeInternals = false
  MapMode = 5
  Placement = pos=(3.73e-14,0,-4) rot=(1,0,0;3.14159rad)
  sketch-geometry (20):
    g0: ArcOfCircle CenterX=-4.3 CenterY=43.65 CenterZ=0 NormalX=0 NormalY=0 NormalZ=1 AngleXU=0 Radius=0.5 StartAngle=3.14158 EndAngle=4.71239
    g1: ArcOfCircle CenterX=-4.3 CenterY=49.65 CenterZ=0 NormalX=0 NormalY=0 NormalZ=1 AngleXU=0 Radius=0.5 StartAngle=1.5708 EndAngle=3.14159
    g2: ArcOfCircle CenterX=1.7 CenterY=43.65 CenterZ=0 NormalX=0 NormalY=0 NormalZ=1 AngleXU=0 Radius=0.5 StartAngle=4.71239 EndAngle=6.28319
    g3: LineSegment StartX=-4.3 StartY=43.15 StartZ=0 EndX=1.7 EndY=43.15 EndZ=0
    g4: LineSegment StartX=-4.8 StartY=43.65 StartZ=0 EndX=-4.8 EndY=49.65 EndZ=0
    g5: LineSegment StartX=-4.3 StartY=50.15 StartZ=0 EndX=0.2 EndY=50.15 EndZ=0
    g6: LineSegment StartX=0.2 StartY=50.15 StartZ=0 EndX=0.2 EndY=79.05 EndZ=0
    g7: LineSegment StartX=1.2 StartY=80.05 StartZ=0 EndX=20.8 EndY=80.05 EndZ=0
    g8: ArcOfCircle CenterX=20.8 CenterY=79.05 CenterZ=0 NormalX=0 NormalY=0 NormalZ=1 AngleXU=0 Radius=1 StartAngle=-1.8e-15 EndAngle=1.5708
    g9: LineSegment StartX=21.8 StartY=79.05 StartZ=0 EndX=21.8 EndY=50.15 EndZ=0
    g10: LineSegment StartX=21.8 StartY=50.15 StartZ=0 EndX=26.3 EndY=50.15 EndZ=0
    g11: ArcOfCircle CenterX=26.3 CenterY=49.65 CenterZ=0 NormalX=0 NormalY=0 NormalZ=1 AngleXU=0 Radius=0.5 StartAngle=6.28319 EndAngle=7.85398
    g12: ArcOfCircle CenterX=26.3 CenterY=43.65 CenterZ=0 NormalX=0 NormalY=0 NormalZ=1 AngleXU=0 Radius=0.5 StartAngle=4.71239 EndAngle=6.28319
    g13: ArcOfCircle CenterX=20.3 CenterY=43.65 CenterZ=0 NormalX=0 NormalY=0 NormalZ=1 AngleXU=0 Radius=0.5 StartAngle=3.14159 EndAngle=4.71239
    g14: LineSegment StartX=26.8 StartY=49.65 StartZ=0 EndX=26.8 EndY=43.65 EndZ=0
    g15: LineSegment StartX=26.3 StartY=43.15 StartZ=0 EndX=20.3 EndY=43.15 EndZ=0
    g16: LineSegment StartX=19.8 StartY=43.65 StartZ=0 EndX=19.8 EndY=78.05 EndZ=0
    g17: LineSegment StartX=19.8 StartY=78.05 StartZ=0 EndX=2.2 EndY=78.05 EndZ=0
    g18: LineSegment StartX=2.2 StartY=43.65 StartZ=0 EndX=2.2 EndY=78.05 EndZ=0
    g19: ArcOfCircle CenterX=1.2 CenterY=79.05 CenterZ=0 NormalX=0 NormalY=0 NormalZ=1 AngleXU=0 Radius=1 StartAngle=1.5708 EndAngle=3.14159
  constraints (44):
    c: Coincident(g0,g-8)
    c: Tangent(g1,g-7) = -1.5708
    c: Coincident(g1,g-7)
    c: Tangent(g2,g-9) = -1.5708
    c: Coincident(g2,g-10)
    c: Tangent(g4,g1) = 1.5708
    c: Coincident(g5,g1)
    c: Coincident(g5,g-6)
    c: Coincident(g6,g5)
    c: Coincident(g6,g-16)
    c: Coincident(g7,g-14)
    c: Coincident(g8,g7)
    c: Coincident(g8,g-15)
    c: Coincident(g9,g8)
    c: Coincident(g9,g-18)
    c: Coincident(g10,g9)
    c: Coincident(g10,g-21)
    c: Coincident(g11,g10)
    c: Tangent(g12,g-23) = -1.5708
    c: Coincident(g12,g-24)
    c: Coincident(g13,g-24)
    c: Tangent(g13,g-20) = -1.5708
    c: Tangent(g14,g12) = 1.5708
    c: Coincident(g15,g12)
    c: Coincident(g15,g13)
    c: Coincident(g16,g13)
    c: Vertical(g16)
    c: Coincident(g17,g16)
    c: Horizontal(g17)
    c: Coincident(g18,g2)
    c: Coincident(g18,g17)
    c: Vertical(g18)
    c: Coincident(g7,g19)
    c: Coincident(g3,g0)
    c: Coincident(g3,g2)
    c: Coincident(g19,g6)
    c: Coincident(g19,g-11)
    c: DistanceX(g7,g19) = 0
    c: DistanceX(g7,g8) = 0
    c: DistanceY(g17,g7) = 2
    c: Coincident(g14,g11)
    c: Coincident(g11,g-21)
    c: Coincident(g4,g0)
    c: Coincident(g0,g-8)
FEATURE [PartDesign::Pad] Pad149
  Direction = (9.3e-15,0,-1)
  Length = 5
  Length2 = 10
  Profile = -> Sketch206
  ReferenceAxis = -> Sketch206 [N_Axis]
  Refine = true
  Suppressed = false
  Type = 0
FEATURE [Sketcher::SketchObject] Sketch207
  ArcFitTolerance = 1e-06
  AttachmentSupport = -> [Pad149]
  ExternalGeometry = -> [Pad149]
  FullyConstrained = true
  MakeInternals = false
  MapMode = 5
  Placement = pos=(-5.84e-14,-80.05,0) rot=(1,0,0;1.5708rad)
  sketch-geometry (2):
    g0: ArcOfCircle CenterX=11 CenterY=-4 CenterZ=0 NormalX=0 NormalY=0 NormalZ=1 AngleXU=0 Radius=3.45 StartAngle=3.14159 EndAngle=6.28319
    g1: LineSegment StartX=7.55 StartY=-4 StartZ=0 EndX=14.45 EndY=-4 EndZ=0
  constraints (7):
    c: PointOnObject(g0,g-3)
    c: PointOnObject(g0,g-3)
    c: Coincident(g1,g0)
    c: Coincident(g1,g0)
    c: PointOnObject(g0,g1)
    c: Diameter(g0) = 6.9
    c: DistanceX(g-5,g0) = 7.35
FEATURE [PartDesign::Pocket] Pocket058
  BaseFeature = -> Pad149
  Direction = (0,1,-2e-16)
  Length = 5
  Length2 = 5
  Profile = -> Sketch207
  ReferenceAxis = -> Sketch207 [N_Axis]
  Refine = true
  Suppressed = false
  Type = 0
FEATURE [Sketcher::SketchObject] Sketch208
  ArcFitTolerance = 1e-06
  AttachmentSupport = -> [Pocket058]
  ExternalGeometry = -> [Pocket058]
  FullyConstrained = true
  MakeInternals = false
  MapMode = 5
  Placement = pos=(8.4e-14,0,-9) rot=(1,0,0;3.14159rad)
  sketch-geometry (6):
    g0: LineSegment StartX=0.2 StartY=79.05 StartZ=0 EndX=0.2 EndY=63.15 EndZ=0
    g1: LineSegment StartX=0.2 StartY=63.15 StartZ=0 EndX=21.8 EndY=63.15 EndZ=0
    g2: ArcOfCircle CenterX=1.2 CenterY=79.05 CenterZ=0 NormalX=0 NormalY=0 NormalZ=1 AngleXU=0 Radius=1 StartAngle=1.5708 EndAngle=3.14159
    g3: ArcOfCircle CenterX=20.8 CenterY=79.05 CenterZ=0 NormalX=0 NormalY=0 NormalZ=1 AngleXU=0 Radius=1 StartAngle=9e-16 EndAngle=1.5708
    g4: LineSegment StartX=1.2 StartY=80.05 StartZ=0 EndX=20.8 EndY=80.05 EndZ=0
    g5: LineSegment StartX=21.8 StartY=79.05 StartZ=0 EndX=21.8 EndY=63.15 EndZ=0
  constraints (15):
    c: Coincident(g0,g-7)
    c: PointOnObject(g0,g-7)
    c: Coincident(g1,g0)
    c: PointOnObject(g1,g-6)
    c: Horizontal(g1)
    c: Coincident(g2,g0)
    c: Coincident(g2,g-4)
    c: Tangent(g3,g-8) = -1.5708
    c: Coincident(g3,g-8)
    c: Coincident(g5,g3)
    c: Coincident(g5,g1)
    c: DistanceY(g1,g4) = 16.9
    c: Coincident(g4,g3)
    c: Coincident(g4,g2)
    c: DistanceX(g2,g2) = 0
FEATURE [PartDesign::Pad] Pad150
  BaseFeature = -> Pocket058
  Direction = (9.3e-15,0,-1)
  Length = 2
  Length2 = 10
  Profile = -> Sketch208
  ReferenceAxis = -> Sketch208 [N_Axis]
  Refine = true
  Suppressed = false
  Type = 0
FEATURE [Sketcher::SketchObject] Sketch209
  ArcFitTolerance = 1e-06
  AttachmentSupport = -> [Pad150]
  ExternalGeometry = -> [Pad150]
  FullyConstrained = true
  MakeInternals = false
  MapMode = 5
  Placement = pos=(3.73e-14,0,-4) rot=(0,0,1;0rad)
  sketch-geometry (8):
    g0: LineSegment StartX=0.2 StartY=-72.55 StartZ=0 EndX=0.2 EndY=-77.15 EndZ=0
    g1: LineSegment StartX=0.2 StartY=-77.15 StartZ=0 EndX=2.2 EndY=-77.15 EndZ=0
    g2: LineSegment StartX=2.2 StartY=-77.15 StartZ=0 EndX=2.2 EndY=-72.55 EndZ=0
    g3: LineSegment StartX=2.2 StartY=-72.55 StartZ=0 EndX=0.2 EndY=-72.55 EndZ=0
    g4: LineSegment StartX=19.8 StartY=-72.55 StartZ=0 EndX=19.8 EndY=-77.15 EndZ=0
    g5: LineSegment StartX=19.8 StartY=-77.15 StartZ=0 EndX=21.8 EndY=-77.15 EndZ=0
    g6: LineSegment StartX=21.8 StartY=-77.15 StartZ=0 EndX=21.8 EndY=-72.55 EndZ=0
    g7: LineSegment StartX=21.8 StartY=-72.55 StartZ=0 EndX=19.8 EndY=-72.55 EndZ=0
  constraints (24):
    c: Coincident(g0,g1)
    c: Coincident(g1,g2)
    c: Coincident(g2,g3)
    c: Coincident(g3,g0)
    c: Vertical(g0)
    c: Vertical(g2)
    c: Horizontal(g1)
    c: Horizontal(g3)
    c: PointOnObject(g1,g-5)
    c: Coincident(g4,g5)
    c: Coincident(g5,g6)
    c: Coincident(g6,g7)
    c: Coincident(g7,g4)
    c: Vertical(g4)
    c: Vertical(g6)
    c: Horizontal(g5)
    c: Horizontal(g7)
    c: PointOnObject(g4,g-4)
    c: PointOnObject(g5,g-3)
    c: DistanceY(g6,g6) = 4.6
    c: DistanceY(g-3,g5) = 1.9
    c: PointOnObject(g0,g-6)
    c: DistanceY(g2,g2) = 4.6
    c: DistanceY(g-6,g0) = 1.9
FEATURE [PartDesign::Pad] Pad151
  BaseFeature = -> Pad150
  Direction = (-9.3e-15,0,1)
  Length = 2
  Length2 = 10
  Profile = -> Sketch209
  ReferenceAxis = -> Sketch209 [N_Axis]
  Refine = true
  Suppressed = false
  Type = 0
FEATURE [Sketcher::SketchObject] Sketch210
  ArcFitTolerance = 1e-06
  AttachmentSupport = -> [Pad151]
  ExternalGeometry = -> [Pad151]
  FullyConstrained = true
  MakeInternals = false
  MapMode = 5
  Placement = pos=(1.023e-13,0,-11) rot=(1,0,0;3.14159rad)
  sketch-geometry (8):
    g0: LineSegment StartX=18 StartY=80.05 StartZ=0 EndX=18 EndY=78.05 EndZ=0
    g1: LineSegment StartX=18 StartY=78.05 StartZ=0 EndX=19.8 EndY=78.05 EndZ=0
    g2: LineSegment StartX=19.8 StartY=78.05 StartZ=0 EndX=19.8 EndY=80.05 EndZ=0
    g3: LineSegment StartX=19.8 StartY=80.05 StartZ=0 EndX=18 EndY=80.05 EndZ=0
    g4: LineSegment StartX=2.2 StartY=80.05 StartZ=0 EndX=2.2 EndY=78.05 EndZ=0
    g5: LineSegment StartX=2.2 StartY=78.05 StartZ=0 EndX=4 EndY=78.05 EndZ=0
    g6: LineSegment StartX=4 StartY=78.05 StartZ=0 EndX=4 EndY=80.05 EndZ=0
    g7: LineSegment StartX=4 StartY=80.05 StartZ=0 EndX=2.2 EndY=80.05 EndZ=0
  constraints (25):
    c: Coincident(g0,g1)
    c: Coincident(g1,g2)
    c: Coincident(g2,g3)
    c: Coincident(g3,g0)
    c: Vertical(g0)
    c: Vertical(g2)
    c: Horizontal(g1)
    c: Horizontal(g3)
    c: PointOnObject(g0,g-3)
    c: Coincident(g4,g5)
    c: Coincident(g5,g6)
    c: Coincident(g6,g7)
    c: Coincident(g7,g4)
    c: Vertical(g4)
    c: Vertical(g6)
    c: Horizontal(g5)
    c: Horizontal(g7)
    c: PointOnObject(g4,g-3)
    c: DistanceX(g7,g7) = 1.8
    c: DistanceX(g3,g3) = 1.8
    c: DistanceX(g-4,g4) = 2
    c: DistanceX(g1,g-5) = 2
    c: DistanceX(g6,g0) = 14
    c: DistanceY(g6,g6) = 2
    c: DistanceY(g0,g0) = 2
FEATURE [PartDesign::Pocket] Pocket207
  BaseFeature = -> Pad151
  Direction = (-9.3e-15,0,1)
  Length = 1.9
  Length2 = 5
  Profile = -> Sketch210
  ReferenceAxis = -> Sketch210 [N_Axis]
  Refine = true
  Suppressed = false
  Type = 0
FEATURE [Sketcher::SketchObject] Sketch211
  ArcFitTolerance = 1e-06
  AttachmentSupport = -> [Pocket207]
  ExternalGeometry = -> [Pocket207]
  FullyConstrained = true
  MakeInternals = false
  MapMode = 5
  Placement = pos=(1.023e-13,0,-11) rot=(1,0,0;3.14159rad)
  sketch-geometry (8):
    g0: LineSegment StartX=-1.5 StartY=70.05 StartZ=0 EndX=-1.5 EndY=67.35 EndZ=0
    g1: LineSegment StartX=-1.5 StartY=67.35 StartZ=0 EndX=2 EndY=67.35 EndZ=0
    g2: LineSegment StartX=2 StartY=67.35 StartZ=0 EndX=2 EndY=70.05 EndZ=0
    g3: LineSegment StartX=2 StartY=70.05 StartZ=0 EndX=-1.5 EndY=70.05 EndZ=0
    g4: LineSegment StartX=20 StartY=70.05 StartZ=0 EndX=20 EndY=67.35 EndZ=0
    g5: LineSegment StartX=20 StartY=67.35 StartZ=0 EndX=23.5 EndY=67.35 EndZ=0
    g6: LineSegment StartX=23.5 StartY=67.35 StartZ=0 EndX=23.5 EndY=70.05 EndZ=0
    g7: LineSegment StartX=23.5 StartY=70.05 StartZ=0 EndX=20 EndY=70.05 EndZ=0
  constraints (24):
    c: Coincident(g0,g1)
    c: Coincident(g1,g2)
    c: Coincident(g2,g3)
    c: Coincident(g3,g0)
    c: Vertical(g0)
    c: Vertical(g2)
    c: Horizontal(g1)
    c: Horizontal(g3)
    c: Coincident(g4,g5)
    c: Coincident(g5,g6)
    c: Coincident(g6,g7)
    c: Coincident(g7,g4)
    c: Vertical(g4)
    c: Vertical(g6)
    c: Horizontal(g5)
    c: Horizontal(g7)
    c: DistanceY(g0,g0) = 2.7
    c: DistanceY(g6,g6) = 2.7
    c: DistanceX(g7,g7) = 3.5
    c: DistanceX(g3,g3) = 3.5
    c: DistanceX(g0,g-4) = 1.7
    c: DistanceX(g-3,g6) = 1.7
    c: DistanceY(g2,g-5) = 10
    c: DistanceY(g4,g-6) = 10
FEATURE [PartDesign::Pad] Pad152
  BaseFeature = -> Pocket207
  Direction = (9.3e-15,0,-1)
  Length = 2
  Length2 = 10
  Profile = -> Sketch211
  ReferenceAxis = -> Sketch211 [N_Axis]
  Refine = true
  Suppressed = false
  Type = 0
FEATURE [Sketcher::SketchObject] Sketch212
  ArcFitTolerance = 1e-06
  AttachmentSupport = -> [Pad152]
  ExternalGeometry = -> [Pad152]
  FullyConstrained = true
  MakeInternals = false
  MapMode = 5
  Placement = pos=(3.73e-14,0,-4) rot=(0,0,1;0rad)
  sketch-geometry (2):
    g0: Circle CenterX=-1.3 CenterY=-46.65 CenterZ=0 NormalX=0 NormalY=0 NormalZ=1 AngleXU=0 Radius=1.95
    g1: Circle CenterX=23.3 CenterY=-46.65 CenterZ=0 NormalX=0 NormalY=0 NormalZ=1 AngleXU=0 Radius=1.95
  constraints (7):
    c: Diameter(g0) = 3.9
    c: Diameter(g1) = 3.9
    c: DistanceX(g-5,g-3) = 7
    c: DistanceX(g-5,g0) = 3.5
    c: DistanceX(g-7,g1) = 3.5
    c: DistanceY(g-10,g1) = 3.5
    c: DistanceY(g-6,g0) = 3.5
FEATURE [PartDesign::Pad] Pad153
  BaseFeature = -> Pad152
  Direction = (-9.3e-15,0,1)
  Length = 2
  Length2 = 10
  Profile = -> Sketch212
  ReferenceAxis = -> Sketch212 [N_Axis]
  Refine = true
  Suppressed = false
  Type = 0
FEATURE [Sketcher::SketchObject] Sketch213
  ArcFitTolerance = 1e-06
  AttachmentSupport = -> [Pad153]
  ExternalGeometry = -> [Pad153]
  FullyConstrained = true
  MakeInternals = false
  MapMode = 5
  Placement = pos=(1.87e-14,0,-2) rot=(0,0,1;0rad)
  sketch-geometry (2):
    g0: Circle CenterX=-1.3 CenterY=-46.65 CenterZ=0 NormalX=0 NormalY=0 NormalZ=1 AngleXU=0 Radius=0.75
    g1: Circle CenterX=23.3 CenterY=-46.65 CenterZ=0 NormalX=0 NormalY=0 NormalZ=1 AngleXU=0 Radius=0.75
  constraints (4):
    c: Coincident(g0,g-4)
    c: Coincident(g1,g-3)
    c: Diameter(g0) = 1.5
    c: Diameter(g1) = 1.5
FEATURE [PartDesign::Pocket] Pocket208
  BaseFeature = -> Pad153
  Direction = (9.3e-15,0,-1)
  Length = 5
  Length2 = 5
  Profile = -> Sketch213
  ReferenceAxis = -> Sketch213 [N_Axis]
  Refine = true
  Suppressed = false
  Type = 0
FEATURE [Sketcher::SketchObject] Sketch214
  ArcFitTolerance = 1e-06
  AttachmentSupport = -> [Pocket208]
  ExternalGeometry = -> [Pocket208]
  FullyConstrained = true
  MakeInternals = false
  MapMode = 5
  Placement = pos=(21.8,-1.18e-14,2.115e-13) rot=(0.57735,0.57735,0.57735;2.0944rad)
  sketch-geometry (8):
    g0: LineSegment StartX=-59.45 StartY=-4 StartZ=0 EndX=-59.45 EndY=-6 EndZ=0
    g1: LineSegment StartX=-58.95 StartY=-6.5 StartZ=0 EndX=-57.9054 EndY=-6.5 EndZ=0
    g2: LineSegment StartX=-57.45 StartY=-6.2064 StartZ=0 EndX=-56.45 EndY=-4 EndZ=0
    g3: ArcOfCircle CenterX=-58.95 CenterY=-6 CenterZ=0 NormalX=0 NormalY=0 NormalZ=1 AngleXU=0 Radius=0.5 StartAngle=3.14159 EndAngle=4.71239
    g4: GeomPoint [constr] X=-59.45 Y=-6.5 Z=0
    g5: ArcOfCircle CenterX=-57.9054 CenterY=-6 CenterZ=0 NormalX=0 NormalY=0 NormalZ=1 AngleXU=0 Radius=0.5 StartAngle=4.71239 EndAngle=5.85765
    g6: GeomPoint [constr] X=-57.5831 Y=-6.5 Z=0
    g7: LineSegment StartX=-59.45 StartY=-4 StartZ=0 EndX=-56.45 EndY=-4 EndZ=0
  constraints (20):
    c: PointOnObject(g0,g-3)
    c: Vertical(g0)
    c: Horizontal(g1)
    c: PointOnObject(g2,g-3)
    c: PointOnObject(g4,g0)
    c: PointOnObject(g4,g1)
    c: Tangent(g0,g3) = -1.5708
    c: Tangent(g1,g3) = -1.5708
    c: PointOnObject(g6,g1)
    c: PointOnObject(g6,g2)
    c: Tangent(g1,g5) = -1.5708
    c: Tangent(g2,g5) = -1.5708
    c: DistanceX(g-4,g0) = 20.6
    c: DistanceX(g-4,g2) = 23.6
    c: Radius(g3) = 0.5
    c: Radius(g5) = 0.5
    c: DistanceX(g0,g2) = 2
    c: DistanceY(g1,g0) = 2.5
    c: Coincident(g7,g0)
    c: Coincident(g7,g2)
FEATURE [PartDesign::Pocket] Pocket209
  BaseFeature = -> Pocket208
  Direction = (-1,0,-9.8e-15)
  Length = 0.75
  Length2 = 5
  Profile = -> Sketch214
  ReferenceAxis = -> Sketch214 [N_Axis]
  Refine = true
  Suppressed = false
  Type = 0
FEATURE [PartDesign::Fillet] Fillet012
  Base = -> Pocket209 [Edge45,Edge44,Edge43,Edge42,Edge41]
  BaseFeature = -> Pocket209
  Radius = 0.5
  Refine = true
  SupportTransform = false
  Suppressed = false
  UseAllEdges = false
FEATURE [Sketcher::SketchObject] Sketch215
  ArcFitTolerance = 1e-06
  AttachmentSupport = -> [Fillet012]
  ExternalGeometry = -> [Fillet012]
  FullyConstrained = true
  MakeInternals = false
  MapMode = 5
  Placement = pos=(0.2,0,1.9e-15) rot=(0.57735,-0.57735,-0.57735;2.0944rad)
  sketch-geometry (8):
    g0: LineSegment StartX=59.45 StartY=-4 StartZ=0 EndX=59.45 EndY=-6 EndZ=0
    g1: LineSegment StartX=58.95 StartY=-6.5 StartZ=0 EndX=57.9054 EndY=-6.5 EndZ=0
    g2: LineSegment StartX=57.45 StartY=-6.2064 StartZ=0 EndX=56.45 EndY=-4 EndZ=0
    g3: ArcOfCircle CenterX=57.9054 CenterY=-6 CenterZ=0 NormalX=0 NormalY=0 NormalZ=1 AngleXU=0 Radius=0.5 StartAngle=3.56713 EndAngle=4.71239
    g4: GeomPoint [constr] X=57.5831 Y=-6.5 Z=0
    g5: ArcOfCircle CenterX=58.95 CenterY=-6 CenterZ=0 NormalX=0 NormalY=0 NormalZ=1 AngleXU=0 Radius=0.5 StartAngle=4.71239 EndAngle=6.28319
    g6: GeomPoint [constr] X=59.45 Y=-6.5 Z=0
    g7: LineSegment StartX=59.45 StartY=-4 StartZ=0 EndX=56.45 EndY=-4 EndZ=0
  constraints (20):
    c: PointOnObject(g0,g-4)
    c: Vertical(g0)
    c: Horizontal(g1)
    c: PointOnObject(g2,g-4)
    c: PointOnObject(g4,g1)
    c: PointOnObject(g4,g2)
    c: Tangent(g1,g3) = 1.5708
    c: Tangent(g2,g3) = 1.5708
    c: PointOnObject(g6,g0)
    c: PointOnObject(g6,g1)
    c: Tangent(g0,g5) = 1.5708
    c: Tangent(g1,g5) = 1.5708
    c: Radius(g5) = 0.5
    c: Radius(g3) = 0.5
    c: DistanceX(g2,g0) = 2
    c: DistanceX(g0,g-3) = 20.6
    c: DistanceY(g1,g0) = 2.5
    c: DistanceX(g2,g0) = 3
    c: Coincident(g7,g0)
    c: Coincident(g7,g2)
FEATURE [PartDesign::Pocket] Pocket210
  BaseFeature = -> Fillet012
  Direction = (1,0,9.3e-15)
  Length = 0.75
  Length2 = 5
  Profile = -> Sketch215
  ReferenceAxis = -> Sketch215 [N_Axis]
  Refine = true
  Suppressed = false
  Type = 0
FEATURE [PartDesign::Fillet] Fillet013
  Base = -> Pocket210 [Edge138,Edge137,Edge136,Edge135,Edge134]
  BaseFeature = -> Pocket210
  Radius = 0.5
  Refine = true
  SupportTransform = false
  Suppressed = false
  UseAllEdges = false
FEATURE [PartDesign::Body] Body020  label="Front Feet"
  AllowCompound = false
  Group = -> [Binder012,Sketch206,Pad149,Sketch207,Pocket058,Sketch208,Pad150,Sketch209,Pad151,Sketch210,Pocket207,Sketch211,Pad152,Sketch212,Pad153,Sketch213,Pocket208,Sketch214,Pocket209,Fillet012,Sketch215,Pocket210,Fillet013]
  Origin = -> Origin022
  Placement = pos=(33,38,0) rot=(0,0,1;0rad)
  Tip = -> Fillet013
